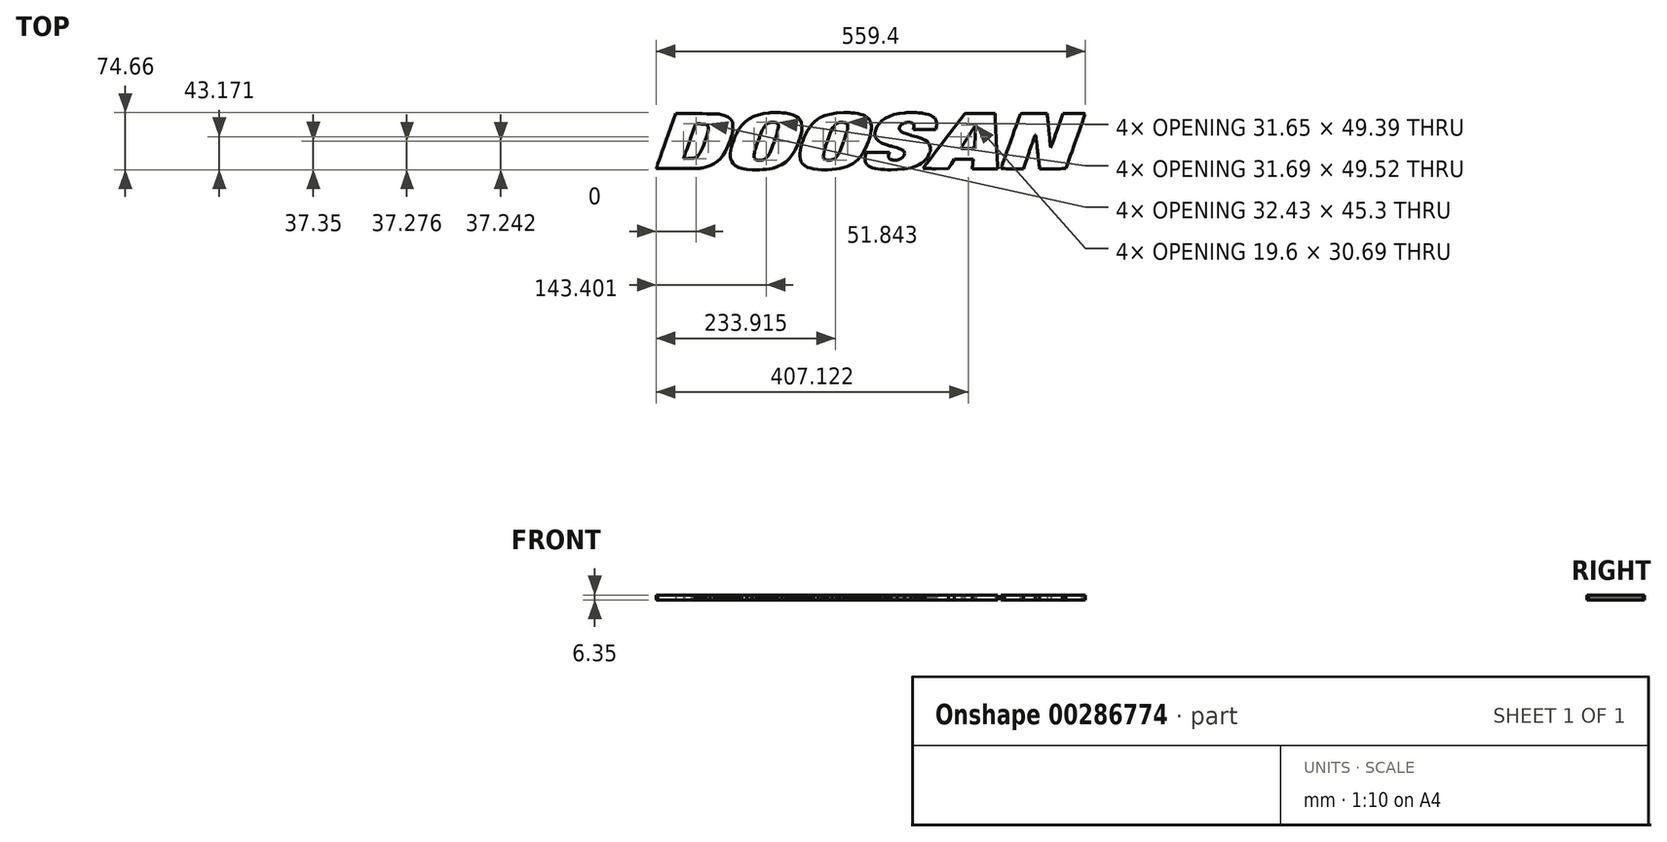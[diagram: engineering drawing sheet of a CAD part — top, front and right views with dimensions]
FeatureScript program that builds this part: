
annotation { "Feature Type Name" : "Feature", "Feature Type Description" : "" }
export const myFeature = defineFeature(function(context is Context, id is Id, definition is map)
    precondition{}
    {
        {
            var Q0;
            Q0=qCreatedBy(makeId("Top.planeOp"),FACE);
            var sketch = newSketch(context, id + "F0", { "sketchPlane" : qUnion([Q0])});
            skLineSegment(sketch, "E0", {"start": v(-105.6, 35.72) * mm, "end": v(-101.05, 34.34) * mm});
            skLineSegment(sketch, "E1", {"start": v(-101.05, 34.34) * mm, "end": v(-97.28, 32.51) * mm});
            skLineSegment(sketch, "E2", {"start": v(-97.28, 32.51) * mm, "end": v(-94.28, 30.22) * mm});
            skLineSegment(sketch, "E3", {"start": v(-94.28, 30.22) * mm, "end": v(-92.03, 27.44) * mm});
            skLineSegment(sketch, "E4", {"start": v(-92.03, 27.44) * mm, "end": v(-90.53, 24.18) * mm});
            skLineSegment(sketch, "E5", {"start": v(-90.53, 24.18) * mm, "end": v(-89.78, 20.43) * mm});
            skLineSegment(sketch, "E6", {"start": v(-89.78, 20.43) * mm, "end": v(-89.67, 17.22) * mm});
            skLineSegment(sketch, "E7", {"start": v(-89.67, 17.22) * mm, "end": v(-89.75, 16.16) * mm});
            skLineSegment(sketch, "E8", {"start": v(-89.75, 16.16) * mm, "end": v(-89.8, 15.4) * mm});
            skLineSegment(sketch, "E9", {"start": v(-89.8, 15.4) * mm, "end": v(-90.08, 13.11) * mm});
            skLineSegment(sketch, "E10", {"start": v(-90.08, 13.11) * mm, "end": v(-90.68, 9.87) * mm});
            skLineSegment(sketch, "E11", {"start": v(-90.68, 9.87) * mm, "end": v(-91.57, 6.31) * mm});
            skLineSegment(sketch, "E12", {"start": v(-91.57, 6.31) * mm, "end": v(-92.46, 3.3) * mm});
            skLineSegment(sketch, "E13", {"start": v(-92.46, 3.3) * mm, "end": v(-92.78, 2.3) * mm});
            skLineSegment(sketch, "E14", {"start": v(-92.78, 2.3) * mm, "end": v(-93.41, 0.35) * mm});
            skLineSegment(sketch, "E15", {"start": v(-93.41, 0.35) * mm, "end": v(-95.6, -5.4) * mm});
            skLineSegment(sketch, "E16", {"start": v(-95.6, -5.4) * mm, "end": v(-98.8, -12.14) * mm});
            skLineSegment(sketch, "E17", {"start": v(-98.8, -12.14) * mm, "end": v(-102.38, -17.98) * mm});
            skLineSegment(sketch, "E18", {"start": v(-102.38, -17.98) * mm, "end": v(-106.4, -22.97) * mm});
            skLineSegment(sketch, "E19", {"start": v(-106.4, -22.97) * mm, "end": v(-110.9, -27.13) * mm});
            skLineSegment(sketch, "E20", {"start": v(-110.9, -27.13) * mm, "end": v(-115.92, -30.5) * mm});
            skLineSegment(sketch, "E21", {"start": v(-115.92, -30.5) * mm, "end": v(-121.5, -33.15) * mm});
            skLineSegment(sketch, "E22", {"start": v(-121.5, -33.15) * mm, "end": v(-126.1, -34.71) * mm});
            skLineSegment(sketch, "E23", {"start": v(-126.1, -34.71) * mm, "end": v(-127.67, -35.1) * mm});
            skLineSegment(sketch, "E24", {"start": v(-127.67, -35.1) * mm, "end": v(-128.72, -35.37) * mm});
            skLineSegment(sketch, "E25", {"start": v(-128.72, -35.37) * mm, "end": v(-131.91, -36.04) * mm});
            skLineSegment(sketch, "E26", {"start": v(-131.91, -36.04) * mm, "end": v(-136.16, -36.67) * mm});
            skLineSegment(sketch, "E27", {"start": v(-136.16, -36.67) * mm, "end": v(-140.94, -37.07) * mm});
            skLineSegment(sketch, "E28", {"start": v(-140.94, -37.07) * mm, "end": v(-145.33, -37.25) * mm});
            skLineSegment(sketch, "E29", {"start": v(-145.33, -37.25) * mm, "end": v(-146.8, -37.29) * mm});
            skLineSegment(sketch, "E30", {"start": v(-146.8, -37.29) * mm, "end": v(-148.82, -37.33) * mm});
            skLineSegment(sketch, "E31", {"start": v(-148.82, -37.33) * mm, "end": v(-154.9, -37.25) * mm});
            skLineSegment(sketch, "E32", {"start": v(-154.9, -37.25) * mm, "end": v(-161.9, -36.73) * mm});
            skLineSegment(sketch, "E33", {"start": v(-161.9, -36.73) * mm, "end": v(-167.81, -35.7) * mm});
            skLineSegment(sketch, "E34", {"start": v(-167.81, -35.7) * mm, "end": v(-172.7, -34.15) * mm});
            skLineSegment(sketch, "E35", {"start": v(-172.7, -34.15) * mm, "end": v(-176.59, -32.06) * mm});
            skLineSegment(sketch, "E36", {"start": v(-176.59, -32.06) * mm, "end": v(-179.53, -29.41) * mm});
            skLineSegment(sketch, "E37", {"start": v(-179.53, -29.41) * mm, "end": v(-181.58, -26.19) * mm});
            skLineSegment(sketch, "E38", {"start": v(-181.58, -26.19) * mm, "end": v(-182.6, -23.34) * mm});
            skLineSegment(sketch, "E39", {"start": v(-182.6, -23.34) * mm, "end": v(-182.78, -22.37) * mm});
            skLineSegment(sketch, "E40", {"start": v(-182.78, -22.37) * mm, "end": v(-182.91, -21.66) * mm});
            skLineSegment(sketch, "E41", {"start": v(-182.91, -21.66) * mm, "end": v(-183.07, -19.48) * mm});
            skLineSegment(sketch, "E42", {"start": v(-183.07, -19.48) * mm, "end": v(-182.97, -16.11) * mm});
            skLineSegment(sketch, "E43", {"start": v(-182.97, -16.11) * mm, "end": v(-182.5, -12.35) * mm});
            skLineSegment(sketch, "E44", {"start": v(-182.5, -12.35) * mm, "end": v(-181.66, -8.26) * mm});
            skLineSegment(sketch, "E45", {"start": v(-181.66, -8.26) * mm, "end": v(-180.48, -3.94) * mm});
            skLineSegment(sketch, "E46", {"start": v(-180.48, -3.94) * mm, "end": v(-178.99, 0.55) * mm});
            skLineSegment(sketch, "E47", {"start": v(-178.99, 0.55) * mm, "end": v(-177.2, 5.13) * mm});
            skLineSegment(sketch, "E48", {"start": v(-177.2, 5.13) * mm, "end": v(-175.67, 8.57) * mm});
            skLineSegment(sketch, "E49", {"start": v(-175.67, 8.57) * mm, "end": v(-175.12, 9.7) * mm});
            skLineSegment(sketch, "E50", {"start": v(-175.12, 9.7) * mm, "end": v(-174.36, 11.28) * mm});
            skLineSegment(sketch, "E51", {"start": v(-174.36, 11.28) * mm, "end": v(-171.72, 15.85) * mm});
            skLineSegment(sketch, "E52", {"start": v(-171.72, 15.85) * mm, "end": v(-167.86, 21.14) * mm});
            skLineSegment(sketch, "E53", {"start": v(-167.86, 21.14) * mm, "end": v(-163.49, 25.62) * mm});
            skLineSegment(sketch, "E54", {"start": v(-163.49, 25.62) * mm, "end": v(-158.53, 29.31) * mm});
            skLineSegment(sketch, "E55", {"start": v(-158.53, 29.31) * mm, "end": v(-152.93, 32.26) * mm});
            skLineSegment(sketch, "E56", {"start": v(-152.93, 32.26) * mm, "end": v(-146.63, 34.51) * mm});
            skLineSegment(sketch, "E57", {"start": v(-146.63, 34.51) * mm, "end": v(-139.57, 36.1) * mm});
            skLineSegment(sketch, "E58", {"start": v(-139.57, 36.1) * mm, "end": v(-133.67, 36.89) * mm});
            skLineSegment(sketch, "E59", {"start": v(-133.67, 36.89) * mm, "end": v(-131.7, 37.04) * mm});
            skLineSegment(sketch, "E60", {"start": v(-131.7, 37.04) * mm, "end": v(-131.18, 37.08) * mm});
            skLineSegment(sketch, "E61", {"start": v(-131.18, 37.08) * mm, "end": v(-129.63, 37.16) * mm});
            skLineSegment(sketch, "E62", {"start": v(-129.63, 37.16) * mm, "end": v(-127.08, 37.22) * mm});
            skLineSegment(sketch, "E63", {"start": v(-127.08, 37.22) * mm, "end": v(-124.2, 37.23) * mm});
            skLineSegment(sketch, "E64", {"start": v(-124.2, 37.23) * mm, "end": v(-121.18, 37.2) * mm});
            skLineSegment(sketch, "E65", {"start": v(-121.18, 37.2) * mm, "end": v(-118.17, 37.11) * mm});
            skLineSegment(sketch, "E66", {"start": v(-118.17, 37.11) * mm, "end": v(-115.35, 37) * mm});
            skLineSegment(sketch, "E67", {"start": v(-115.35, 37) * mm, "end": v(-112.88, 36.84) * mm});
            skLineSegment(sketch, "E68", {"start": v(-112.88, 36.84) * mm, "end": v(-111.43, 36.71) * mm});
            skLineSegment(sketch, "E69", {"start": v(-111.43, 36.71) * mm, "end": v(-110.95, 36.65) * mm});
            skLineSegment(sketch, "E70", {"start": v(-25.01, 37.04) * mm, "end": v(-23.91, 36.96) * mm});
            skLineSegment(sketch, "E71", {"start": v(-23.91, 36.96) * mm, "end": v(-20.62, 36.62) * mm});
            skLineSegment(sketch, "E72", {"start": v(-20.62, 36.62) * mm, "end": v(-16.65, 36) * mm});
            skLineSegment(sketch, "E73", {"start": v(-16.65, 36) * mm, "end": v(-13.1, 35.16) * mm});
            skLineSegment(sketch, "E74", {"start": v(-13.1, 35.16) * mm, "end": v(-9.97, 34.1) * mm});
            skLineSegment(sketch, "E75", {"start": v(-9.97, 34.1) * mm, "end": v(-7.26, 32.82) * mm});
            skLineSegment(sketch, "E76", {"start": v(-7.26, 32.82) * mm, "end": v(-4.94, 31.3) * mm});
            skLineSegment(sketch, "E77", {"start": v(-4.94, 31.3) * mm, "end": v(-3.02, 29.55) * mm});
            skLineSegment(sketch, "E78", {"start": v(-3.02, 29.55) * mm, "end": v(-1.5, 27.53) * mm});
            skLineSegment(sketch, "E79", {"start": v(-1.5, 27.53) * mm, "end": v(-0.35, 25.24) * mm});
            skLineSegment(sketch, "E80", {"start": v(-0.35, 25.24) * mm, "end": v(0.41, 22.68) * mm});
            skLineSegment(sketch, "E81", {"start": v(0.41, 22.68) * mm, "end": v(0.8, 19.84) * mm});
            skLineSegment(sketch, "E82", {"start": v(0.8, 19.84) * mm, "end": v(0.81, 16.7) * mm});
            skLineSegment(sketch, "E83", {"start": v(0.81, 16.7) * mm, "end": v(0.47, 13.26) * mm});
            skLineSegment(sketch, "E84", {"start": v(0.47, 13.26) * mm, "end": v(-0.23, 9.5) * mm});
            skLineSegment(sketch, "E85", {"start": v(-0.23, 9.5) * mm, "end": v(-1.28, 5.43) * mm});
            skLineSegment(sketch, "E86", {"start": v(-1.28, 5.43) * mm, "end": v(-2.3, 2.12) * mm});
            skLineSegment(sketch, "E87", {"start": v(-2.3, 2.12) * mm, "end": v(-2.68, 1.02) * mm});
            skLineSegment(sketch, "E88", {"start": v(-2.68, 1.02) * mm, "end": v(-3.13, -0.3) * mm});
            skLineSegment(sketch, "E89", {"start": v(-3.13, -0.3) * mm, "end": v(-4.62, -4.21) * mm});
            skLineSegment(sketch, "E90", {"start": v(-4.62, -4.21) * mm, "end": v(-6.7, -9.02) * mm});
            skLineSegment(sketch, "E91", {"start": v(-6.7, -9.02) * mm, "end": v(-8.97, -13.4) * mm});
            skLineSegment(sketch, "E92", {"start": v(-8.97, -13.4) * mm, "end": v(-11.42, -17.36) * mm});
            skLineSegment(sketch, "E93", {"start": v(-11.42, -17.36) * mm, "end": v(-14.08, -20.94) * mm});
            skLineSegment(sketch, "E94", {"start": v(-14.08, -20.94) * mm, "end": v(-16.97, -24.12) * mm});
            skLineSegment(sketch, "E95", {"start": v(-16.97, -24.12) * mm, "end": v(-20.1, -26.93) * mm});
            skLineSegment(sketch, "E96", {"start": v(-20.1, -26.93) * mm, "end": v(-23.5, -29.38) * mm});
            skLineSegment(sketch, "E97", {"start": v(-23.5, -29.38) * mm, "end": v(-27.17, -31.47) * mm});
            skLineSegment(sketch, "E98", {"start": v(-27.17, -31.47) * mm, "end": v(-31.14, -33.23) * mm});
            skLineSegment(sketch, "E99", {"start": v(-31.14, -33.23) * mm, "end": v(-35.43, -34.65) * mm});
            skLineSegment(sketch, "E100", {"start": v(-35.43, -34.65) * mm, "end": v(-40.05, -35.77) * mm});
            skLineSegment(sketch, "E101", {"start": v(-40.05, -35.77) * mm, "end": v(-45.03, -36.57) * mm});
            skLineSegment(sketch, "E102", {"start": v(-45.03, -36.57) * mm, "end": v(-50.38, -37.09) * mm});
            skLineSegment(sketch, "E103", {"start": v(-50.38, -37.09) * mm, "end": v(-56.12, -37.32) * mm});
            skLineSegment(sketch, "E104", {"start": v(-56.12, -37.32) * mm, "end": v(-60.73, -37.33) * mm});
            skLineSegment(sketch, "E105", {"start": v(-60.73, -37.33) * mm, "end": v(-62.27, -37.29) * mm});
            skLineSegment(sketch, "E106", {"start": v(-62.27, -37.29) * mm, "end": v(-64, -37.24) * mm});
            skLineSegment(sketch, "E107", {"start": v(-64, -37.24) * mm, "end": v(-69.22, -36.94) * mm});
            skLineSegment(sketch, "E108", {"start": v(-69.22, -36.94) * mm, "end": v(-74.68, -36.29) * mm});
            skLineSegment(sketch, "E109", {"start": v(-74.68, -36.29) * mm, "end": v(-79.14, -35.24) * mm});
            skLineSegment(sketch, "E110", {"start": v(-79.14, -35.24) * mm, "end": v(-82.13, -34.17) * mm});
            skLineSegment(sketch, "E111", {"start": v(-82.13, -34.17) * mm, "end": v(-83.08, -33.73) * mm});
            skLineSegment(sketch, "E112", {"start": v(-83.08, -33.73) * mm, "end": v(-83.6, -33.48) * mm});
            skLineSegment(sketch, "E113", {"start": v(-83.6, -33.48) * mm, "end": v(-85.13, -32.65) * mm});
            skLineSegment(sketch, "E114", {"start": v(-85.13, -32.65) * mm, "end": v(-86.84, -31.48) * mm});
            skLineSegment(sketch, "E115", {"start": v(-86.84, -31.48) * mm, "end": v(-88.32, -30.13) * mm});
            skLineSegment(sketch, "E116", {"start": v(-88.32, -30.13) * mm, "end": v(-89.36, -28.95) * mm});
            skLineSegment(sketch, "E117", {"start": v(-89.36, -28.95) * mm, "end": v(-89.68, -28.54) * mm});
            skLineSegment(sketch, "E118", {"start": v(-89.68, -28.54) * mm, "end": v(-90.1, -27.99) * mm});
            skLineSegment(sketch, "E119", {"start": v(-90.1, -27.99) * mm, "end": v(-91.08, -26.13) * mm});
            skLineSegment(sketch, "E120", {"start": v(-91.08, -26.13) * mm, "end": v(-92, -23.28) * mm});
            skLineSegment(sketch, "E121", {"start": v(-92, -23.28) * mm, "end": v(-92.46, -19.99) * mm});
            skLineSegment(sketch, "E122", {"start": v(-92.46, -19.99) * mm, "end": v(-92.44, -16.27) * mm});
            skLineSegment(sketch, "E123", {"start": v(-92.44, -16.27) * mm, "end": v(-91.95, -12.14) * mm});
            skLineSegment(sketch, "E124", {"start": v(-91.95, -12.14) * mm, "end": v(-91, -7.6) * mm});
            skLineSegment(sketch, "E125", {"start": v(-91, -7.6) * mm, "end": v(-89.56, -2.65) * mm});
            skLineSegment(sketch, "E126", {"start": v(-89.56, -2.65) * mm, "end": v(-88.17, 1.36) * mm});
            skLineSegment(sketch, "E127", {"start": v(-88.17, 1.36) * mm, "end": v(-87.67, 2.68) * mm});
            skLineSegment(sketch, "E128", {"start": v(-87.67, 2.68) * mm, "end": v(-87.11, 4.1) * mm});
            skLineSegment(sketch, "E129", {"start": v(-87.11, 4.1) * mm, "end": v(-85.27, 8.3) * mm});
            skLineSegment(sketch, "E130", {"start": v(-85.27, 8.3) * mm, "end": v(-82.64, 13.37) * mm});
            skLineSegment(sketch, "E131", {"start": v(-82.64, 13.37) * mm, "end": v(-79.77, 17.89) * mm});
            skLineSegment(sketch, "E132", {"start": v(-79.77, 17.89) * mm, "end": v(-76.65, 21.87) * mm});
            skLineSegment(sketch, "E133", {"start": v(-76.65, 21.87) * mm, "end": v(-73.26, 25.33) * mm});
            skLineSegment(sketch, "E134", {"start": v(-73.26, 25.33) * mm, "end": v(-69.59, 28.3) * mm});
            skLineSegment(sketch, "E135", {"start": v(-69.59, 28.3) * mm, "end": v(-65.62, 30.77) * mm});
            skLineSegment(sketch, "E136", {"start": v(-65.62, 30.77) * mm, "end": v(-62.44, 32.34) * mm});
            skLineSegment(sketch, "E137", {"start": v(-62.44, 32.34) * mm, "end": v(-61.35, 32.77) * mm});
            skLineSegment(sketch, "E138", {"start": v(-61.35, 32.77) * mm, "end": v(-59.5, 33.51) * mm});
            skLineSegment(sketch, "E139", {"start": v(-59.5, 33.51) * mm, "end": v(-53.74, 35.13) * mm});
            skLineSegment(sketch, "E140", {"start": v(-53.74, 35.13) * mm, "end": v(-44.87, 36.65) * mm});
            skLineSegment(sketch, "E141", {"start": v(-44.87, 36.65) * mm, "end": v(-35.17, 37.3) * mm});
            skLineSegment(sketch, "E142", {"start": v(-35.17, 37.3) * mm, "end": v(-27.54, 37.23) * mm});
            skLineSegment(sketch, "E143", {"start": v(-27.54, 37.23) * mm, "end": v(-25.01, 37.04) * mm});
            skLineSegment(sketch, "E144", {"start": v(67.06, 36.51) * mm, "end": v(68.19, 36.37) * mm});
            skLineSegment(sketch, "E145", {"start": v(68.19, 36.37) * mm, "end": v(71.54, 35.76) * mm});
            skLineSegment(sketch, "E146", {"start": v(71.54, 35.76) * mm, "end": v(75.38, 34.76) * mm});
            skLineSegment(sketch, "E147", {"start": v(75.38, 34.76) * mm, "end": v(78.61, 33.49) * mm});
            skLineSegment(sketch, "E148", {"start": v(78.61, 33.49) * mm, "end": v(81.24, 31.94) * mm});
            skLineSegment(sketch, "E149", {"start": v(81.24, 31.94) * mm, "end": v(83.27, 30.13) * mm});
            skLineSegment(sketch, "E150", {"start": v(83.27, 30.13) * mm, "end": v(84.7, 28.02) * mm});
            skLineSegment(sketch, "E151", {"start": v(84.7, 28.02) * mm, "end": v(85.57, 25.62) * mm});
            skLineSegment(sketch, "E152", {"start": v(85.57, 25.62) * mm, "end": v(85.86, 23.6) * mm});
            skLineSegment(sketch, "E153", {"start": v(85.86, 23.6) * mm, "end": v(85.87, 22.93) * mm});
            skLineSegment(sketch, "E154", {"start": v(85.87, 22.93) * mm, "end": v(85.87, 22.62) * mm});
            skLineSegment(sketch, "E155", {"start": v(85.87, 22.62) * mm, "end": v(85.83, 21.7) * mm});
            skLineSegment(sketch, "E156", {"start": v(85.83, 21.7) * mm, "end": v(85.7, 20.31) * mm});
            skLineSegment(sketch, "E157", {"start": v(85.7, 20.31) * mm, "end": v(85.5, 18.94) * mm});
            skLineSegment(sketch, "E158", {"start": v(85.5, 18.94) * mm, "end": v(85.31, 18.04) * mm});
            skLineSegment(sketch, "E159", {"start": v(85.31, 18.04) * mm, "end": v(85.23, 17.75) * mm});
            skLineSegment(sketch, "E160", {"start": v(85.23, 17.75) * mm, "end": v(84.6, 15.17) * mm});
            skLineSegment(sketch, "E161", {"start": v(84.6, 15.17) * mm, "end": v(69.96, 15.17) * mm});
            skLineSegment(sketch, "E162", {"start": v(69.96, 15.17) * mm, "end": v(68.8, 15.17) * mm});
            skLineSegment(sketch, "E163", {"start": v(68.8, 15.17) * mm, "end": v(65.37, 15.17) * mm});
            skLineSegment(sketch, "E164", {"start": v(65.37, 15.17) * mm, "end": v(61.85, 15.18) * mm});
            skLineSegment(sketch, "E165", {"start": v(61.85, 15.18) * mm, "end": v(59.27, 15.21) * mm});
            skLineSegment(sketch, "E166", {"start": v(59.27, 15.21) * mm, "end": v(57.5, 15.26) * mm});
            skLineSegment(sketch, "E167", {"start": v(57.5, 15.26) * mm, "end": v(56.37, 15.34) * mm});
            skLineSegment(sketch, "E168", {"start": v(56.37, 15.34) * mm, "end": v(55.77, 15.45) * mm});
            skLineSegment(sketch, "E169", {"start": v(55.77, 15.45) * mm, "end": v(55.54, 15.6) * mm});
            skLineSegment(sketch, "E170", {"start": v(55.54, 15.6) * mm, "end": v(55.54, 15.76) * mm});
            skLineSegment(sketch, "E171", {"start": v(55.54, 15.76) * mm, "end": v(55.56, 15.8) * mm});
            skLineSegment(sketch, "E172", {"start": v(55.56, 15.8) * mm, "end": v(55.77, 16.3) * mm});
            skLineSegment(sketch, "E173", {"start": v(55.77, 16.3) * mm, "end": v(56.2, 17.9) * mm});
            skLineSegment(sketch, "E174", {"start": v(56.2, 17.9) * mm, "end": v(56.39, 19.84) * mm});
            skLineSegment(sketch, "E175", {"start": v(56.39, 19.84) * mm, "end": v(56.11, 21.5) * mm});
            skLineSegment(sketch, "E176", {"start": v(56.11, 21.5) * mm, "end": v(55.63, 22.5) * mm});
            skLineSegment(sketch, "E177", {"start": v(55.63, 22.5) * mm, "end": v(55.39, 22.75) * mm});
            skLineSegment(sketch, "E178", {"start": v(55.39, 22.75) * mm, "end": v(55.13, 23.03) * mm});
            skLineSegment(sketch, "E179", {"start": v(55.13, 23.03) * mm, "end": v(54.19, 23.71) * mm});
            skLineSegment(sketch, "E180", {"start": v(54.19, 23.71) * mm, "end": v(52.67, 24.33) * mm});
            skLineSegment(sketch, "E181", {"start": v(52.67, 24.33) * mm, "end": v(50.75, 24.62) * mm});
            skLineSegment(sketch, "E182", {"start": v(50.75, 24.62) * mm, "end": v(48.96, 24.65) * mm});
            skLineSegment(sketch, "E183", {"start": v(48.96, 24.65) * mm, "end": v(48.37, 24.62) * mm});
            skLineSegment(sketch, "E184", {"start": v(48.37, 24.62) * mm, "end": v(47.8, 24.6) * mm});
            skLineSegment(sketch, "E185", {"start": v(47.8, 24.6) * mm, "end": v(46.1, 24.35) * mm});
            skLineSegment(sketch, "E186", {"start": v(46.1, 24.35) * mm, "end": v(44.02, 23.8) * mm});
            skLineSegment(sketch, "E187", {"start": v(44.02, 23.8) * mm, "end": v(42.15, 23.03) * mm});
            skLineSegment(sketch, "E188", {"start": v(42.15, 23.03) * mm, "end": v(40.54, 22.04) * mm});
            skLineSegment(sketch, "E189", {"start": v(40.54, 22.04) * mm, "end": v(39.22, 20.87) * mm});
            skLineSegment(sketch, "E190", {"start": v(39.22, 20.87) * mm, "end": v(38.23, 19.54) * mm});
            skLineSegment(sketch, "E191", {"start": v(38.23, 19.54) * mm, "end": v(37.6, 18.1) * mm});
            skLineSegment(sketch, "E192", {"start": v(37.6, 18.1) * mm, "end": v(37.4, 16.93) * mm});
            skLineSegment(sketch, "E193", {"start": v(37.4, 16.93) * mm, "end": v(37.4, 16.54) * mm});
            skLineSegment(sketch, "E194", {"start": v(37.4, 16.54) * mm, "end": v(37.4, 16.22) * mm});
            skLineSegment(sketch, "E195", {"start": v(37.4, 16.22) * mm, "end": v(37.55, 15.24) * mm});
            skLineSegment(sketch, "E196", {"start": v(37.55, 15.24) * mm, "end": v(38.09, 14.07) * mm});
            skLineSegment(sketch, "E197", {"start": v(38.09, 14.07) * mm, "end": v(39.07, 12.99) * mm});
            skLineSegment(sketch, "E198", {"start": v(39.07, 12.99) * mm, "end": v(40.58, 11.96) * mm});
            skLineSegment(sketch, "E199", {"start": v(40.58, 11.96) * mm, "end": v(42.7, 10.93) * mm});
            skLineSegment(sketch, "E200", {"start": v(42.7, 10.93) * mm, "end": v(45.5, 9.86) * mm});
            skLineSegment(sketch, "E201", {"start": v(45.5, 9.86) * mm, "end": v(49.07, 8.72) * mm});
            skLineSegment(sketch, "E202", {"start": v(49.07, 8.72) * mm, "end": v(52.38, 7.75) * mm});
            skLineSegment(sketch, "E203", {"start": v(52.38, 7.75) * mm, "end": v(53.48, 7.44) * mm});
            skLineSegment(sketch, "E204", {"start": v(53.48, 7.44) * mm, "end": v(54.33, 7.2) * mm});
            skLineSegment(sketch, "E205", {"start": v(54.33, 7.2) * mm, "end": v(56.87, 6.48) * mm});
            skLineSegment(sketch, "E206", {"start": v(56.87, 6.48) * mm, "end": v(59.67, 5.67) * mm});
            skLineSegment(sketch, "E207", {"start": v(59.67, 5.67) * mm, "end": v(61.97, 4.96) * mm});
            skLineSegment(sketch, "E208", {"start": v(61.97, 4.96) * mm, "end": v(63.88, 4.33) * mm});
            skLineSegment(sketch, "E209", {"start": v(63.88, 4.33) * mm, "end": v(65.52, 3.73) * mm});
            skLineSegment(sketch, "E210", {"start": v(65.52, 3.73) * mm, "end": v(66.98, 3.12) * mm});
            skLineSegment(sketch, "E211", {"start": v(66.98, 3.12) * mm, "end": v(68.38, 2.48) * mm});
            skLineSegment(sketch, "E212", {"start": v(68.38, 2.48) * mm, "end": v(69.46, 1.95) * mm});
            skLineSegment(sketch, "E213", {"start": v(69.46, 1.95) * mm, "end": v(69.81, 1.76) * mm});
            skLineSegment(sketch, "E214", {"start": v(69.81, 1.76) * mm, "end": v(70.9, 1.2) * mm});
            skLineSegment(sketch, "E215", {"start": v(70.9, 1.2) * mm, "end": v(73.88, -1) * mm});
            skLineSegment(sketch, "E216", {"start": v(73.88, -1) * mm, "end": v(76.54, -4.3) * mm});
            skLineSegment(sketch, "E217", {"start": v(76.54, -4.3) * mm, "end": v(77.8, -8.1) * mm});
            skLineSegment(sketch, "E218", {"start": v(77.8, -8.1) * mm, "end": v(77.81, -11.37) * mm});
            skLineSegment(sketch, "E219", {"start": v(77.81, -11.37) * mm, "end": v(77.61, -12.42) * mm});
            skLineSegment(sketch, "E220", {"start": v(77.61, -12.42) * mm, "end": v(77.46, -13.21) * mm});
            skLineSegment(sketch, "E221", {"start": v(77.46, -13.21) * mm, "end": v(76.75, -15.55) * mm});
            skLineSegment(sketch, "E222", {"start": v(76.75, -15.55) * mm, "end": v(75.44, -18.56) * mm});
            skLineSegment(sketch, "E223", {"start": v(75.44, -18.56) * mm, "end": v(73.7, -21.4) * mm});
            skLineSegment(sketch, "E224", {"start": v(73.7, -21.4) * mm, "end": v(71.57, -24.07) * mm});
            skLineSegment(sketch, "E225", {"start": v(71.57, -24.07) * mm, "end": v(69.06, -26.51) * mm});
            skLineSegment(sketch, "E226", {"start": v(69.06, -26.51) * mm, "end": v(66.2, -28.72) * mm});
            skLineSegment(sketch, "E227", {"start": v(66.2, -28.72) * mm, "end": v(63.02, -30.65) * mm});
            skLineSegment(sketch, "E228", {"start": v(63.02, -30.65) * mm, "end": v(60.44, -31.92) * mm});
            skLineSegment(sketch, "E229", {"start": v(60.44, -31.92) * mm, "end": v(59.55, -32.28) * mm});
            skLineSegment(sketch, "E230", {"start": v(59.55, -32.28) * mm, "end": v(57.74, -33) * mm});
            skLineSegment(sketch, "E231", {"start": v(57.74, -33) * mm, "end": v(52.12, -34.72) * mm});
            skLineSegment(sketch, "E232", {"start": v(52.12, -34.72) * mm, "end": v(43.8, -36.34) * mm});
            skLineSegment(sketch, "E233", {"start": v(43.8, -36.34) * mm, "end": v(34.28, -37.19) * mm});
            skLineSegment(sketch, "E234", {"start": v(34.28, -37.19) * mm, "end": v(26.03, -37.35) * mm});
            skLineSegment(sketch, "E235", {"start": v(26.03, -37.35) * mm, "end": v(23.28, -37.29) * mm});
            skLineSegment(sketch, "E236", {"start": v(23.28, -37.29) * mm, "end": v(21.93, -37.26) * mm});
            skLineSegment(sketch, "E237", {"start": v(21.93, -37.26) * mm, "end": v(17.87, -37.09) * mm});
            skLineSegment(sketch, "E238", {"start": v(17.87, -37.09) * mm, "end": v(13.12, -36.74) * mm});
            skLineSegment(sketch, "E239", {"start": v(13.12, -36.74) * mm, "end": v(8.96, -36.24) * mm});
            skLineSegment(sketch, "E240", {"start": v(8.96, -36.24) * mm, "end": v(5.37, -35.57) * mm});
            skLineSegment(sketch, "E241", {"start": v(5.37, -35.57) * mm, "end": v(2.27, -34.71) * mm});
            skLineSegment(sketch, "E242", {"start": v(2.27, -34.71) * mm, "end": v(-0.37, -33.67) * mm});
            skLineSegment(sketch, "E243", {"start": v(-0.37, -33.67) * mm, "end": v(-2.6, -32.41) * mm});
            skLineSegment(sketch, "E244", {"start": v(-2.6, -32.41) * mm, "end": v(-4.04, -31.34) * mm});
            skLineSegment(sketch, "E245", {"start": v(-4.04, -31.34) * mm, "end": v(-4.48, -30.94) * mm});
            skLineSegment(sketch, "E246", {"start": v(-4.48, -30.94) * mm, "end": v(-4.9, -30.56) * mm});
            skLineSegment(sketch, "E247", {"start": v(-4.9, -30.56) * mm, "end": v(-6.02, -29.33) * mm});
            skLineSegment(sketch, "E248", {"start": v(-6.02, -29.33) * mm, "end": v(-6.97, -27.74) * mm});
            skLineSegment(sketch, "E249", {"start": v(-6.97, -27.74) * mm, "end": v(-7.45, -25.88) * mm});
            skLineSegment(sketch, "E250", {"start": v(-7.45, -25.88) * mm, "end": v(-7.59, -24.06) * mm});
            skLineSegment(sketch, "E251", {"start": v(-7.59, -24.06) * mm, "end": v(-7.59, -23.46) * mm});
            skLineSegment(sketch, "E252", {"start": v(-7.59, -23.46) * mm, "end": v(-7.59, -22.69) * mm});
            skLineSegment(sketch, "E253", {"start": v(-7.59, -22.69) * mm, "end": v(-7.4, -20.38) * mm});
            skLineSegment(sketch, "E254", {"start": v(-7.4, -20.38) * mm, "end": v(-6.9, -18.05) * mm});
            skLineSegment(sketch, "E255", {"start": v(-6.9, -18.05) * mm, "end": v(-6.74, -17.53) * mm});
            skLineSegment(sketch, "E256", {"start": v(-6.74, -17.53) * mm, "end": v(-5.86, -14.82) * mm});
            skLineSegment(sketch, "E257", {"start": v(-5.86, -14.82) * mm, "end": v(9.24, -14.82) * mm});
            skLineSegment(sketch, "E258", {"start": v(9.24, -14.82) * mm, "end": v(10.7, -14.82) * mm});
            skLineSegment(sketch, "E259", {"start": v(10.7, -14.82) * mm, "end": v(15.1, -14.82) * mm});
            skLineSegment(sketch, "E260", {"start": v(15.1, -14.82) * mm, "end": v(19.9, -14.84) * mm});
            skLineSegment(sketch, "E261", {"start": v(19.9, -14.84) * mm, "end": v(23.15, -14.86) * mm});
            skLineSegment(sketch, "E262", {"start": v(23.15, -14.86) * mm, "end": v(24.34, -14.88) * mm});
            skLineSegment(sketch, "E263", {"start": v(24.34, -14.88) * mm, "end": v(24.34, -14.89) * mm});
            skLineSegment(sketch, "E264", {"start": v(24.34, -14.89) * mm, "end": v(24.34, -15) * mm});
            skLineSegment(sketch, "E265", {"start": v(24.34, -15) * mm, "end": v(24.18, -15.38) * mm});
            skLineSegment(sketch, "E266", {"start": v(24.18, -15.38) * mm, "end": v(23.88, -16.2) * mm});
            skLineSegment(sketch, "E267", {"start": v(23.88, -16.2) * mm, "end": v(23.81, -16.4) * mm});
            skLineSegment(sketch, "E268", {"start": v(23.81, -16.4) * mm, "end": v(23.7, -16.75) * mm});
            skLineSegment(sketch, "E269", {"start": v(23.7, -16.75) * mm, "end": v(23.46, -17.84) * mm});
            skLineSegment(sketch, "E270", {"start": v(23.46, -17.84) * mm, "end": v(23.32, -19.41) * mm});
            skLineSegment(sketch, "E271", {"start": v(23.32, -19.41) * mm, "end": v(23.4, -20.89) * mm});
            skLineSegment(sketch, "E272", {"start": v(23.4, -20.89) * mm, "end": v(23.58, -21.78) * mm});
            skLineSegment(sketch, "E273", {"start": v(23.58, -21.78) * mm, "end": v(23.7, -22.05) * mm});
            skLineSegment(sketch, "E274", {"start": v(23.7, -22.05) * mm, "end": v(23.84, -22.34) * mm});
            skLineSegment(sketch, "E275", {"start": v(23.84, -22.34) * mm, "end": v(24.51, -23.1) * mm});
            skLineSegment(sketch, "E276", {"start": v(24.51, -23.1) * mm, "end": v(25.81, -23.93) * mm});
            skLineSegment(sketch, "E277", {"start": v(25.81, -23.93) * mm, "end": v(27.5, -24.5) * mm});
            skLineSegment(sketch, "E278", {"start": v(27.5, -24.5) * mm, "end": v(29.48, -24.81) * mm});
            skLineSegment(sketch, "E279", {"start": v(29.48, -24.81) * mm, "end": v(31.65, -24.86) * mm});
            skLineSegment(sketch, "E280", {"start": v(31.65, -24.86) * mm, "end": v(33.9, -24.63) * mm});
            skLineSegment(sketch, "E281", {"start": v(33.9, -24.63) * mm, "end": v(36.15, -24.12) * mm});
            skLineSegment(sketch, "E282", {"start": v(36.15, -24.12) * mm, "end": v(37.76, -23.56) * mm});
            skLineSegment(sketch, "E283", {"start": v(37.76, -23.56) * mm, "end": v(38.28, -23.32) * mm});
            skLineSegment(sketch, "E284", {"start": v(38.28, -23.32) * mm, "end": v(39.15, -22.91) * mm});
            skLineSegment(sketch, "E285", {"start": v(39.15, -22.91) * mm, "end": v(41.52, -21.16) * mm});
            skLineSegment(sketch, "E286", {"start": v(41.52, -21.16) * mm, "end": v(43.5, -18.5) * mm});
            skLineSegment(sketch, "E287", {"start": v(43.5, -18.5) * mm, "end": v(44.06, -15.72) * mm});
            skLineSegment(sketch, "E288", {"start": v(44.06, -15.72) * mm, "end": v(43.43, -13.71) * mm});
            skLineSegment(sketch, "E289", {"start": v(43.43, -13.71) * mm, "end": v(43, -13.23) * mm});
            skLineSegment(sketch, "E290", {"start": v(43, -13.23) * mm, "end": v(42.8, -13) * mm});
            skLineSegment(sketch, "E291", {"start": v(42.8, -13) * mm, "end": v(42.15, -12.36) * mm});
            skLineSegment(sketch, "E292", {"start": v(42.15, -12.36) * mm, "end": v(41.17, -11.59) * mm});
            skLineSegment(sketch, "E293", {"start": v(41.17, -11.59) * mm, "end": v(39.96, -10.87) * mm});
            skLineSegment(sketch, "E294", {"start": v(39.96, -10.87) * mm, "end": v(38.43, -10.16) * mm});
            skLineSegment(sketch, "E295", {"start": v(38.43, -10.16) * mm, "end": v(36.48, -9.42) * mm});
            skLineSegment(sketch, "E296", {"start": v(36.48, -9.42) * mm, "end": v(34.02, -8.63) * mm});
            skLineSegment(sketch, "E297", {"start": v(34.02, -8.63) * mm, "end": v(30.95, -7.72) * mm});
            skLineSegment(sketch, "E298", {"start": v(30.95, -7.72) * mm, "end": v(28.1, -6.92) * mm});
            skLineSegment(sketch, "E299", {"start": v(28.1, -6.92) * mm, "end": v(27.16, -6.67) * mm});
            skLineSegment(sketch, "E300", {"start": v(27.16, -6.67) * mm, "end": v(25.34, -6.17) * mm});
            skLineSegment(sketch, "E301", {"start": v(25.34, -6.17) * mm, "end": v(19.9, -4.49) * mm});
            skLineSegment(sketch, "E302", {"start": v(19.9, -4.49) * mm, "end": v(14.52, -2.39) * mm});
            skLineSegment(sketch, "E303", {"start": v(14.52, -2.39) * mm, "end": v(10.63, -0.2) * mm});
            skLineSegment(sketch, "E304", {"start": v(10.63, -0.2) * mm, "end": v(8.47, 1.57) * mm});
            skLineSegment(sketch, "E305", {"start": v(8.47, 1.57) * mm, "end": v(7.87, 2.26) * mm});
            skLineSegment(sketch, "E306", {"start": v(7.87, 2.26) * mm, "end": v(7.39, 2.8) * mm});
            skLineSegment(sketch, "E307", {"start": v(7.39, 2.8) * mm, "end": v(6.26, 4.7) * mm});
            skLineSegment(sketch, "E308", {"start": v(6.26, 4.7) * mm, "end": v(5.41, 7.5) * mm});
            skLineSegment(sketch, "E309", {"start": v(5.41, 7.5) * mm, "end": v(5.34, 10.6) * mm});
            skLineSegment(sketch, "E310", {"start": v(5.34, 10.6) * mm, "end": v(5.78, 13.15) * mm});
            skLineSegment(sketch, "E311", {"start": v(5.78, 13.15) * mm, "end": v(6.03, 13.97) * mm});
            skLineSegment(sketch, "E312", {"start": v(6.03, 13.97) * mm, "end": v(6.4, 15.2) * mm});
            skLineSegment(sketch, "E313", {"start": v(6.4, 15.2) * mm, "end": v(8, 18.77) * mm});
            skLineSegment(sketch, "E314", {"start": v(8, 18.77) * mm, "end": v(10.81, 23.02) * mm});
            skLineSegment(sketch, "E315", {"start": v(10.81, 23.02) * mm, "end": v(14.46, 26.72) * mm});
            skLineSegment(sketch, "E316", {"start": v(14.46, 26.72) * mm, "end": v(18.94, 29.89) * mm});
            skLineSegment(sketch, "E317", {"start": v(18.94, 29.89) * mm, "end": v(24.26, 32.5) * mm});
            skLineSegment(sketch, "E318", {"start": v(24.26, 32.5) * mm, "end": v(30.41, 34.56) * mm});
            skLineSegment(sketch, "E319", {"start": v(30.41, 34.56) * mm, "end": v(37.39, 36.08) * mm});
            skLineSegment(sketch, "E320", {"start": v(37.39, 36.08) * mm, "end": v(43.23, 36.88) * mm});
            skLineSegment(sketch, "E321", {"start": v(43.23, 36.88) * mm, "end": v(45.2, 37.04) * mm});
            skLineSegment(sketch, "E322", {"start": v(45.2, 37.04) * mm, "end": v(45.73, 37.09) * mm});
            skLineSegment(sketch, "E323", {"start": v(45.73, 37.09) * mm, "end": v(47.36, 37.17) * mm});
            skLineSegment(sketch, "E324", {"start": v(47.36, 37.17) * mm, "end": v(50.02, 37.23) * mm});
            skLineSegment(sketch, "E325", {"start": v(50.02, 37.23) * mm, "end": v(53, 37.24) * mm});
            skLineSegment(sketch, "E326", {"start": v(53, 37.24) * mm, "end": v(56.14, 37.19) * mm});
            skLineSegment(sketch, "E327", {"start": v(56.14, 37.19) * mm, "end": v(59.28, 37.09) * mm});
            skLineSegment(sketch, "E328", {"start": v(59.28, 37.09) * mm, "end": v(62.25, 36.94) * mm});
            skLineSegment(sketch, "E329", {"start": v(62.25, 36.94) * mm, "end": v(64.9, 36.75) * mm});
            skLineSegment(sketch, "E330", {"start": v(64.9, 36.75) * mm, "end": v(66.52, 36.59) * mm});
            skLineSegment(sketch, "E331", {"start": v(66.52, 36.59) * mm, "end": v(67.06, 36.51) * mm});
            skLineSegment(sketch, "E332", {"start": v(-197.56, 35.17) * mm, "end": v(-196.01, 34.9) * mm});
            skLineSegment(sketch, "E333", {"start": v(-196.01, 34.9) * mm, "end": v(-191.44, 33.75) * mm});
            skLineSegment(sketch, "E334", {"start": v(-191.44, 33.75) * mm, "end": v(-186.71, 31.76) * mm});
            skLineSegment(sketch, "E335", {"start": v(-186.71, 31.76) * mm, "end": v(-183.23, 29.14) * mm});
            skLineSegment(sketch, "E336", {"start": v(-183.23, 29.14) * mm, "end": v(-181.32, 26.7) * mm});
            skLineSegment(sketch, "E337", {"start": v(-181.32, 26.7) * mm, "end": v(-180.87, 25.79) * mm});
            skLineSegment(sketch, "E338", {"start": v(-180.87, 25.79) * mm, "end": v(-180.7, 25.44) * mm});
            skLineSegment(sketch, "E339", {"start": v(-180.7, 25.44) * mm, "end": v(-180.22, 24.37) * mm});
            skLineSegment(sketch, "E340", {"start": v(-180.22, 24.37) * mm, "end": v(-179.88, 23.12) * mm});
            skLineSegment(sketch, "E341", {"start": v(-179.88, 23.12) * mm, "end": v(-179.76, 21.39) * mm});
            skLineSegment(sketch, "E342", {"start": v(-179.76, 21.39) * mm, "end": v(-179.74, 19.24) * mm});
            skLineSegment(sketch, "E343", {"start": v(-179.74, 19.24) * mm, "end": v(-179.74, 18.52) * mm});
            skLineSegment(sketch, "E344", {"start": v(-179.74, 18.52) * mm, "end": v(-179.75, 17.85) * mm});
            skLineSegment(sketch, "E345", {"start": v(-179.75, 17.85) * mm, "end": v(-179.8, 15.83) * mm});
            skLineSegment(sketch, "E346", {"start": v(-179.8, 15.83) * mm, "end": v(-179.94, 13.82) * mm});
            skLineSegment(sketch, "E347", {"start": v(-179.94, 13.82) * mm, "end": v(-180.24, 12.02) * mm});
            skLineSegment(sketch, "E348", {"start": v(-180.24, 12.02) * mm, "end": v(-180.6, 10.49) * mm});
            skLineSegment(sketch, "E349", {"start": v(-180.6, 10.49) * mm, "end": v(-180.73, 9.98) * mm});
            skLineSegment(sketch, "E350", {"start": v(-180.73, 9.98) * mm, "end": v(-180.98, 9.02) * mm});
            skLineSegment(sketch, "E351", {"start": v(-180.98, 9.02) * mm, "end": v(-181.86, 6.16) * mm});
            skLineSegment(sketch, "E352", {"start": v(-181.86, 6.16) * mm, "end": v(-183.43, 1.41) * mm});
            skLineSegment(sketch, "E353", {"start": v(-183.43, 1.41) * mm, "end": v(-185.15, -3.44) * mm});
            skLineSegment(sketch, "E354", {"start": v(-185.15, -3.44) * mm, "end": v(-186.34, -6.56) * mm});
            skLineSegment(sketch, "E355", {"start": v(-186.34, -6.56) * mm, "end": v(-186.76, -7.58) * mm});
            skLineSegment(sketch, "E356", {"start": v(-186.76, -7.58) * mm, "end": v(-187.38, -9.08) * mm});
            skLineSegment(sketch, "E357", {"start": v(-187.38, -9.08) * mm, "end": v(-189.48, -13.45) * mm});
            skLineSegment(sketch, "E358", {"start": v(-189.48, -13.45) * mm, "end": v(-192.52, -18.5) * mm});
            skLineSegment(sketch, "E359", {"start": v(-192.52, -18.5) * mm, "end": v(-195.93, -22.81) * mm});
            skLineSegment(sketch, "E360", {"start": v(-195.93, -22.81) * mm, "end": v(-199.8, -26.43) * mm});
            skLineSegment(sketch, "E361", {"start": v(-199.8, -26.43) * mm, "end": v(-204.18, -29.42) * mm});
            skLineSegment(sketch, "E362", {"start": v(-204.18, -29.42) * mm, "end": v(-209.17, -31.83) * mm});
            skLineSegment(sketch, "E363", {"start": v(-209.17, -31.83) * mm, "end": v(-214.81, -33.73) * mm});
            skLineSegment(sketch, "E364", {"start": v(-214.81, -33.73) * mm, "end": v(-219.59, -34.88) * mm});
            skLineSegment(sketch, "E365", {"start": v(-219.59, -34.88) * mm, "end": v(-221.2, -35.17) * mm});
            skLineSegment(sketch, "E366", {"start": v(-221.2, -35.17) * mm, "end": v(-221.49, -35.22) * mm});
            skLineSegment(sketch, "E367", {"start": v(-221.49, -35.22) * mm, "end": v(-222.37, -35.35) * mm});
            skLineSegment(sketch, "E368", {"start": v(-222.37, -35.35) * mm, "end": v(-223.86, -35.49) * mm});
            skLineSegment(sketch, "E369", {"start": v(-223.86, -35.49) * mm, "end": v(-225.9, -35.6) * mm});
            skLineSegment(sketch, "E370", {"start": v(-225.9, -35.6) * mm, "end": v(-228.7, -35.68) * mm});
            skLineSegment(sketch, "E371", {"start": v(-228.7, -35.68) * mm, "end": v(-232.5, -35.75) * mm});
            skLineSegment(sketch, "E372", {"start": v(-232.5, -35.75) * mm, "end": v(-237.51, -35.8) * mm});
            skLineSegment(sketch, "E373", {"start": v(-237.51, -35.8) * mm, "end": v(-243.98, -35.84) * mm});
            skLineSegment(sketch, "E374", {"start": v(-243.98, -35.84) * mm, "end": v(-250.1, -35.87) * mm});
            skLineSegment(sketch, "E375", {"start": v(-250.1, -35.87) * mm, "end": v(-252.13, -35.88) * mm});
            skLineSegment(sketch, "E376", {"start": v(-252.13, -35.88) * mm, "end": v(-253.52, -35.88) * mm});
            skLineSegment(sketch, "E377", {"start": v(-253.52, -35.88) * mm, "end": v(-257.68, -35.9) * mm});
            skLineSegment(sketch, "E378", {"start": v(-257.68, -35.9) * mm, "end": v(-262.86, -35.9) * mm});
            skLineSegment(sketch, "E379", {"start": v(-262.86, -35.9) * mm, "end": v(-267.55, -35.9) * mm});
            skLineSegment(sketch, "E380", {"start": v(-267.55, -35.9) * mm, "end": v(-271.64, -35.89) * mm});
            skLineSegment(sketch, "E381", {"start": v(-271.64, -35.89) * mm, "end": v(-275.02, -35.86) * mm});
            skLineSegment(sketch, "E382", {"start": v(-275.02, -35.86) * mm, "end": v(-277.58, -35.83) * mm});
            skLineSegment(sketch, "E383", {"start": v(-277.58, -35.83) * mm, "end": v(-279.2, -35.78) * mm});
            skLineSegment(sketch, "E384", {"start": v(-279.2, -35.78) * mm, "end": v(-279.75, -35.75) * mm});
            skLineSegment(sketch, "E385", {"start": v(-279.75, -35.75) * mm, "end": v(-279.75, -35.74) * mm});
            skLineSegment(sketch, "E386", {"start": v(-279.75, -35.74) * mm, "end": v(-279.75, -35.54) * mm});
            skLineSegment(sketch, "E387", {"start": v(-279.75, -35.54) * mm, "end": v(-279.5, -34.95) * mm});
            skLineSegment(sketch, "E388", {"start": v(-279.5, -34.95) * mm, "end": v(-278.76, -32.81) * mm});
            skLineSegment(sketch, "E389", {"start": v(-278.76, -32.81) * mm, "end": v(-277.6, -29.46) * mm});
            skLineSegment(sketch, "E390", {"start": v(-277.6, -29.46) * mm, "end": v(-276.05, -25.04) * mm});
            skLineSegment(sketch, "E391", {"start": v(-276.05, -25.04) * mm, "end": v(-274.18, -19.71) * mm});
            skLineSegment(sketch, "E392", {"start": v(-274.18, -19.71) * mm, "end": v(-272.04, -13.61) * mm});
            skLineSegment(sketch, "E393", {"start": v(-272.04, -13.61) * mm, "end": v(-269.69, -6.9) * mm});
            skLineSegment(sketch, "E394", {"start": v(-269.69, -6.9) * mm, "end": v(-267.8, -1.51) * mm});
            skLineSegment(sketch, "E395", {"start": v(-267.8, -1.51) * mm, "end": v(-267.16, 0.28) * mm});
            skLineSegment(sketch, "E396", {"start": v(-267.16, 0.28) * mm, "end": v(-254.53, 36.02) * mm});
            skLineSegment(sketch, "E397", {"start": v(-254.53, 36.02) * mm, "end": v(-227.72, 35.88) * mm});
            skLineSegment(sketch, "E398", {"start": v(-227.72, 35.88) * mm, "end": v(-225.8, 35.87) * mm});
            skLineSegment(sketch, "E399", {"start": v(-225.8, 35.87) * mm, "end": v(-220.04, 35.84) * mm});
            skLineSegment(sketch, "E400", {"start": v(-220.04, 35.84) * mm, "end": v(-213.85, 35.8) * mm});
            skLineSegment(sketch, "E401", {"start": v(-213.85, 35.8) * mm, "end": v(-208.97, 35.74) * mm});
            skLineSegment(sketch, "E402", {"start": v(-208.97, 35.74) * mm, "end": v(-205.2, 35.67) * mm});
            skLineSegment(sketch, "E403", {"start": v(-205.2, 35.67) * mm, "end": v(-202.37, 35.59) * mm});
            skLineSegment(sketch, "E404", {"start": v(-202.37, 35.59) * mm, "end": v(-200.27, 35.48) * mm});
            skLineSegment(sketch, "E405", {"start": v(-200.27, 35.48) * mm, "end": v(-198.73, 35.34) * mm});
            skLineSegment(sketch, "E406", {"start": v(-198.73, 35.34) * mm, "end": v(-197.85, 35.22) * mm});
            skLineSegment(sketch, "E407", {"start": v(-197.85, 35.22) * mm, "end": v(-197.56, 35.17) * mm});
            skLineSegment(sketch, "E408", {"start": v(161.92, 34.64) * mm, "end": v(161.92, 34.4) * mm});
            skLineSegment(sketch, "E409", {"start": v(161.92, 34.4) * mm, "end": v(161.96, 33.67) * mm});
            skLineSegment(sketch, "E410", {"start": v(161.96, 33.67) * mm, "end": v(162.07, 31.43) * mm});
            skLineSegment(sketch, "E411", {"start": v(162.07, 31.43) * mm, "end": v(162.23, 28.08) * mm});
            skLineSegment(sketch, "E412", {"start": v(162.23, 28.08) * mm, "end": v(162.45, 23.74) * mm});
            skLineSegment(sketch, "E413", {"start": v(162.45, 23.74) * mm, "end": v(162.71, 18.56) * mm});
            skLineSegment(sketch, "E414", {"start": v(162.71, 18.56) * mm, "end": v(163.01, 12.7) * mm});
            skLineSegment(sketch, "E415", {"start": v(163.01, 12.7) * mm, "end": v(163.34, 6.29) * mm});
            skLineSegment(sketch, "E416", {"start": v(163.34, 6.29) * mm, "end": v(163.6, 1.18) * mm});
            skLineSegment(sketch, "E417", {"start": v(163.6, 1.18) * mm, "end": v(163.69, -0.53) * mm});
            skLineSegment(sketch, "E418", {"start": v(163.69, -0.53) * mm, "end": v(163.78, -2.23) * mm});
            skLineSegment(sketch, "E419", {"start": v(163.78, -2.23) * mm, "end": v(164.05, -7.34) * mm});
            skLineSegment(sketch, "E420", {"start": v(164.05, -7.34) * mm, "end": v(164.38, -13.72) * mm});
            skLineSegment(sketch, "E421", {"start": v(164.38, -13.72) * mm, "end": v(164.68, -19.54) * mm});
            skLineSegment(sketch, "E422", {"start": v(164.68, -19.54) * mm, "end": v(164.94, -24.65) * mm});
            skLineSegment(sketch, "E423", {"start": v(164.94, -24.65) * mm, "end": v(165.16, -28.9) * mm});
            skLineSegment(sketch, "E424", {"start": v(165.16, -28.9) * mm, "end": v(165.31, -32.18) * mm});
            skLineSegment(sketch, "E425", {"start": v(165.31, -32.18) * mm, "end": v(165.42, -34.31) * mm});
            skLineSegment(sketch, "E426", {"start": v(165.42, -34.31) * mm, "end": v(165.45, -34.96) * mm});
            skLineSegment(sketch, "E427", {"start": v(165.45, -34.96) * mm, "end": v(165.45, -35.17) * mm});
            skLineSegment(sketch, "E428", {"start": v(165.45, -35.17) * mm, "end": v(165.45, -35.98) * mm});
            skLineSegment(sketch, "E429", {"start": v(165.45, -35.98) * mm, "end": v(132.3, -35.98) * mm});
            skLineSegment(sketch, "E430", {"start": v(132.3, -35.98) * mm, "end": v(132.43, -35.17) * mm});
            skLineSegment(sketch, "E431", {"start": v(132.43, -35.17) * mm, "end": v(132.46, -35.07) * mm});
            skLineSegment(sketch, "E432", {"start": v(132.46, -35.07) * mm, "end": v(132.53, -34.54) * mm});
            skLineSegment(sketch, "E433", {"start": v(132.53, -34.54) * mm, "end": v(132.68, -33.38) * mm});
            skLineSegment(sketch, "E434", {"start": v(132.68, -33.38) * mm, "end": v(132.84, -31.87) * mm});
            skLineSegment(sketch, "E435", {"start": v(132.84, -31.87) * mm, "end": v(132.96, -30.59) * mm});
            skLineSegment(sketch, "E436", {"start": v(132.96, -30.59) * mm, "end": v(133, -30.16) * mm});
            skLineSegment(sketch, "E437", {"start": v(133, -30.16) * mm, "end": v(133.04, -29.72) * mm});
            skLineSegment(sketch, "E438", {"start": v(133.04, -29.72) * mm, "end": v(133.16, -28.41) * mm});
            skLineSegment(sketch, "E439", {"start": v(133.16, -28.41) * mm, "end": v(133.32, -26.78) * mm});
            skLineSegment(sketch, "E440", {"start": v(133.32, -26.78) * mm, "end": v(133.46, -25.46) * mm});
            skLineSegment(sketch, "E441", {"start": v(133.46, -25.46) * mm, "end": v(133.53, -24.8) * mm});
            skLineSegment(sketch, "E442", {"start": v(133.53, -24.8) * mm, "end": v(133.56, -24.62) * mm});
            skLineSegment(sketch, "E443", {"start": v(133.56, -24.62) * mm, "end": v(133.77, -23.28) * mm});
            skLineSegment(sketch, "E444", {"start": v(133.77, -23.28) * mm, "end": v(108.7, -23.28) * mm});
            skLineSegment(sketch, "E445", {"start": v(108.7, -23.28) * mm, "end": v(104.88, -29.63) * mm});
            skLineSegment(sketch, "E446", {"start": v(104.88, -29.63) * mm, "end": v(101.07, -35.95) * mm});
            skLineSegment(sketch, "E447", {"start": v(101.07, -35.95) * mm, "end": v(84.56, -35.98) * mm});
            skLineSegment(sketch, "E448", {"start": v(84.56, -35.98) * mm, "end": v(83.73, -35.98) * mm});
            skLineSegment(sketch, "E449", {"start": v(83.73, -35.98) * mm, "end": v(81.24, -35.98) * mm});
            skLineSegment(sketch, "E450", {"start": v(81.24, -35.98) * mm, "end": v(78.15, -35.96) * mm});
            skLineSegment(sketch, "E451", {"start": v(78.15, -35.96) * mm, "end": v(75.35, -35.93) * mm});
            skLineSegment(sketch, "E452", {"start": v(75.35, -35.93) * mm, "end": v(72.92, -35.9) * mm});
            skLineSegment(sketch, "E453", {"start": v(72.92, -35.9) * mm, "end": v(70.92, -35.85) * mm});
            skLineSegment(sketch, "E454", {"start": v(70.92, -35.85) * mm, "end": v(69.4, -35.8) * mm});
            skLineSegment(sketch, "E455", {"start": v(69.4, -35.8) * mm, "end": v(68.47, -35.75) * mm});
            skLineSegment(sketch, "E456", {"start": v(68.47, -35.75) * mm, "end": v(68.16, -35.7) * mm});
            skLineSegment(sketch, "E457", {"start": v(68.16, -35.7) * mm, "end": v(68.17, -35.66) * mm});
            skLineSegment(sketch, "E458", {"start": v(68.17, -35.66) * mm, "end": v(68.73, -34.9) * mm});
            skLineSegment(sketch, "E459", {"start": v(68.73, -34.9) * mm, "end": v(70.34, -32.76) * mm});
            skLineSegment(sketch, "E460", {"start": v(70.34, -32.76) * mm, "end": v(72.87, -29.4) * mm});
            skLineSegment(sketch, "E461", {"start": v(72.87, -29.4) * mm, "end": v(76.2, -25) * mm});
            skLineSegment(sketch, "E462", {"start": v(76.2, -25) * mm, "end": v(80.24, -19.68) * mm});
            skLineSegment(sketch, "E463", {"start": v(80.24, -19.68) * mm, "end": v(84.86, -13.59) * mm});
            skLineSegment(sketch, "E464", {"start": v(84.86, -13.59) * mm, "end": v(89.96, -6.89) * mm});
            skLineSegment(sketch, "E465", {"start": v(89.96, -6.89) * mm, "end": v(94.06, -1.5) * mm});
            skLineSegment(sketch, "E466", {"start": v(94.06, -1.5) * mm, "end": v(95.43, 0.28) * mm});
            skLineSegment(sketch, "E467", {"start": v(95.43, 0.28) * mm, "end": v(122.55, 35.98) * mm});
            skLineSegment(sketch, "E468", {"start": v(122.55, 35.98) * mm, "end": v(161.92, 35.98) * mm});
            skLineSegment(sketch, "E469", {"start": v(161.92, 35.98) * mm, "end": v(161.92, 34.64) * mm});
            skLineSegment(sketch, "E470", {"start": v(230.12, 34.5) * mm, "end": v(230.14, 34.32) * mm});
            skLineSegment(sketch, "E471", {"start": v(230.14, 34.32) * mm, "end": v(230.2, 33.77) * mm});
            skLineSegment(sketch, "E472", {"start": v(230.2, 33.77) * mm, "end": v(230.35, 32.27) * mm});
            skLineSegment(sketch, "E473", {"start": v(230.35, 32.27) * mm, "end": v(230.57, 30.1) * mm});
            skLineSegment(sketch, "E474", {"start": v(230.57, 30.1) * mm, "end": v(230.84, 27.34) * mm});
            skLineSegment(sketch, "E475", {"start": v(230.84, 27.34) * mm, "end": v(231.17, 24.09) * mm});
            skLineSegment(sketch, "E476", {"start": v(231.17, 24.09) * mm, "end": v(231.53, 20.42) * mm});
            skLineSegment(sketch, "E477", {"start": v(231.53, 20.42) * mm, "end": v(231.92, 16.45) * mm});
            skLineSegment(sketch, "E478", {"start": v(231.92, 16.45) * mm, "end": v(232.23, 13.3) * mm});
            skLineSegment(sketch, "E479", {"start": v(232.23, 13.3) * mm, "end": v(232.34, 12.24) * mm});
            skLineSegment(sketch, "E480", {"start": v(232.34, 12.24) * mm, "end": v(232.44, 11.2) * mm});
            skLineSegment(sketch, "E481", {"start": v(232.44, 11.2) * mm, "end": v(232.76, 8.08) * mm});
            skLineSegment(sketch, "E482", {"start": v(232.76, 8.08) * mm, "end": v(233.17, 4.2) * mm});
            skLineSegment(sketch, "E483", {"start": v(233.17, 4.2) * mm, "end": v(233.55, 0.7) * mm});
            skLineSegment(sketch, "E484", {"start": v(233.55, 0.7) * mm, "end": v(233.9, -2.36) * mm});
            skLineSegment(sketch, "E485", {"start": v(233.9, -2.36) * mm, "end": v(234.2, -4.88) * mm});
            skLineSegment(sketch, "E486", {"start": v(234.2, -4.88) * mm, "end": v(234.43, -6.77) * mm});
            skLineSegment(sketch, "E487", {"start": v(234.43, -6.77) * mm, "end": v(234.6, -7.96) * mm});
            skLineSegment(sketch, "E488", {"start": v(234.6, -7.96) * mm, "end": v(234.7, -8.36) * mm});
            skLineSegment(sketch, "E489", {"start": v(234.7, -8.36) * mm, "end": v(234.75, -8.35) * mm});
            skLineSegment(sketch, "E490", {"start": v(234.75, -8.35) * mm, "end": v(234.93, -7.9) * mm});
            skLineSegment(sketch, "E491", {"start": v(234.93, -7.9) * mm, "end": v(235.44, -6.58) * mm});
            skLineSegment(sketch, "E492", {"start": v(235.44, -6.58) * mm, "end": v(236.22, -4.52) * mm});
            skLineSegment(sketch, "E493", {"start": v(236.22, -4.52) * mm, "end": v(237.23, -1.8) * mm});
            skLineSegment(sketch, "E494", {"start": v(237.23, -1.8) * mm, "end": v(238.43, 1.5) * mm});
            skLineSegment(sketch, "E495", {"start": v(238.43, 1.5) * mm, "end": v(239.78, 5.26) * mm});
            skLineSegment(sketch, "E496", {"start": v(239.78, 5.26) * mm, "end": v(241.27, 9.42) * mm});
            skLineSegment(sketch, "E497", {"start": v(241.27, 9.42) * mm, "end": v(242.46, 12.75) * mm});
            skLineSegment(sketch, "E498", {"start": v(242.46, 12.75) * mm, "end": v(242.85, 13.86) * mm});
            skLineSegment(sketch, "E499", {"start": v(242.85, 13.86) * mm, "end": v(250.65, 35.98) * mm});
            skLineSegment(sketch, "E500", {"start": v(250.65, 35.98) * mm, "end": v(265.25, 35.98) * mm});
            skLineSegment(sketch, "E501", {"start": v(265.25, 35.98) * mm, "end": v(266.23, 35.98) * mm});
            skLineSegment(sketch, "E502", {"start": v(266.23, 35.98) * mm, "end": v(269.18, 35.98) * mm});
            skLineSegment(sketch, "E503", {"start": v(269.18, 35.98) * mm, "end": v(272.37, 35.96) * mm});
            skLineSegment(sketch, "E504", {"start": v(272.37, 35.96) * mm, "end": v(274.9, 35.93) * mm});
            skLineSegment(sketch, "E505", {"start": v(274.9, 35.93) * mm, "end": v(276.81, 35.9) * mm});
            skLineSegment(sketch, "E506", {"start": v(276.81, 35.9) * mm, "end": v(278.19, 35.83) * mm});
            skLineSegment(sketch, "E507", {"start": v(278.19, 35.83) * mm, "end": v(279.08, 35.76) * mm});
            skLineSegment(sketch, "E508", {"start": v(279.08, 35.76) * mm, "end": v(279.54, 35.67) * mm});
            skLineSegment(sketch, "E509", {"start": v(279.54, 35.67) * mm, "end": v(279.65, 35.57) * mm});
            skLineSegment(sketch, "E510", {"start": v(279.65, 35.57) * mm, "end": v(279.65, 35.56) * mm});
            skLineSegment(sketch, "E511", {"start": v(279.65, 35.56) * mm, "end": v(279.63, 35.5) * mm});
            skLineSegment(sketch, "E512", {"start": v(279.63, 35.5) * mm, "end": v(279.37, 34.76) * mm});
            skLineSegment(sketch, "E513", {"start": v(279.37, 34.76) * mm, "end": v(278.62, 32.63) * mm});
            skLineSegment(sketch, "E514", {"start": v(278.62, 32.63) * mm, "end": v(277.45, 29.33) * mm});
            skLineSegment(sketch, "E515", {"start": v(277.45, 29.33) * mm, "end": v(275.91, 24.99) * mm});
            skLineSegment(sketch, "E516", {"start": v(275.91, 24.99) * mm, "end": v(274.06, 19.76) * mm});
            skLineSegment(sketch, "E517", {"start": v(274.06, 19.76) * mm, "end": v(271.94, 13.78) * mm});
            skLineSegment(sketch, "E518", {"start": v(271.94, 13.78) * mm, "end": v(269.61, 7.2) * mm});
            skLineSegment(sketch, "E519", {"start": v(269.61, 7.2) * mm, "end": v(267.74, 1.93) * mm});
            skLineSegment(sketch, "E520", {"start": v(267.74, 1.93) * mm, "end": v(267.12, 0.18) * mm});
            skLineSegment(sketch, "E521", {"start": v(267.12, 0.18) * mm, "end": v(266.5, -1.58) * mm});
            skLineSegment(sketch, "E522", {"start": v(266.5, -1.58) * mm, "end": v(264.63, -6.86) * mm});
            skLineSegment(sketch, "E523", {"start": v(264.63, -6.86) * mm, "end": v(262.3, -13.44) * mm});
            skLineSegment(sketch, "E524", {"start": v(262.3, -13.44) * mm, "end": v(260.17, -19.43) * mm});
            skLineSegment(sketch, "E525", {"start": v(260.17, -19.43) * mm, "end": v(258.31, -24.68) * mm});
            skLineSegment(sketch, "E526", {"start": v(258.31, -24.68) * mm, "end": v(256.76, -29.04) * mm});
            skLineSegment(sketch, "E527", {"start": v(256.76, -29.04) * mm, "end": v(255.58, -32.37) * mm});
            skLineSegment(sketch, "E528", {"start": v(255.58, -32.37) * mm, "end": v(254.82, -34.52) * mm});
            skLineSegment(sketch, "E529", {"start": v(254.82, -34.52) * mm, "end": v(254.55, -35.27) * mm});
            skLineSegment(sketch, "E530", {"start": v(254.55, -35.27) * mm, "end": v(254.53, -35.35) * mm});
            skLineSegment(sketch, "E531", {"start": v(254.53, -35.35) * mm, "end": v(254.5, -35.4) * mm});
            skLineSegment(sketch, "E532", {"start": v(254.5, -35.4) * mm, "end": v(254.37, -35.55) * mm});
            skLineSegment(sketch, "E533", {"start": v(254.37, -35.55) * mm, "end": v(253.96, -35.7) * mm});
            skLineSegment(sketch, "E534", {"start": v(253.96, -35.7) * mm, "end": v(253.15, -35.81) * mm});
            skLineSegment(sketch, "E535", {"start": v(253.15, -35.81) * mm, "end": v(251.76, -35.89) * mm});
            skLineSegment(sketch, "E536", {"start": v(251.76, -35.89) * mm, "end": v(249.64, -35.94) * mm});
            skLineSegment(sketch, "E537", {"start": v(249.64, -35.94) * mm, "end": v(246.62, -35.97) * mm});
            skLineSegment(sketch, "E538", {"start": v(246.62, -35.97) * mm, "end": v(242.54, -35.98) * mm});
            skLineSegment(sketch, "E539", {"start": v(242.54, -35.98) * mm, "end": v(238.57, -35.98) * mm});
            skLineSegment(sketch, "E540", {"start": v(238.57, -35.98) * mm, "end": v(237.24, -35.98) * mm});
            skLineSegment(sketch, "E541", {"start": v(237.24, -35.98) * mm, "end": v(220.2, -35.98) * mm});
            skLineSegment(sketch, "E542", {"start": v(220.2, -35.98) * mm, "end": v(220, -35.03) * mm});
            skLineSegment(sketch, "E543", {"start": v(220, -35.03) * mm, "end": v(219.96, -34.89) * mm});
            skLineSegment(sketch, "E544", {"start": v(219.96, -34.89) * mm, "end": v(219.9, -34.4) * mm});
            skLineSegment(sketch, "E545", {"start": v(219.9, -34.4) * mm, "end": v(219.73, -33) * mm});
            skLineSegment(sketch, "E546", {"start": v(219.73, -33) * mm, "end": v(219.49, -30.9) * mm});
            skLineSegment(sketch, "E547", {"start": v(219.49, -30.9) * mm, "end": v(219.18, -28.2) * mm});
            skLineSegment(sketch, "E548", {"start": v(219.18, -28.2) * mm, "end": v(218.8, -25) * mm});
            skLineSegment(sketch, "E549", {"start": v(218.8, -25) * mm, "end": v(218.4, -21.38) * mm});
            skLineSegment(sketch, "E550", {"start": v(218.4, -21.38) * mm, "end": v(217.95, -17.42) * mm});
            skLineSegment(sketch, "E551", {"start": v(217.95, -17.42) * mm, "end": v(217.6, -14.28) * mm});
            skLineSegment(sketch, "E552", {"start": v(217.6, -14.28) * mm, "end": v(217.49, -13.23) * mm});
            skLineSegment(sketch, "E553", {"start": v(217.49, -13.23) * mm, "end": v(217.37, -12.18) * mm});
            skLineSegment(sketch, "E554", {"start": v(217.37, -12.18) * mm, "end": v(217, -9.03) * mm});
            skLineSegment(sketch, "E555", {"start": v(217, -9.03) * mm, "end": v(216.56, -5.1) * mm});
            skLineSegment(sketch, "E556", {"start": v(216.56, -5.1) * mm, "end": v(216.14, -1.51) * mm});
            skLineSegment(sketch, "E557", {"start": v(216.14, -1.51) * mm, "end": v(215.77, 1.64) * mm});
            skLineSegment(sketch, "E558", {"start": v(215.77, 1.64) * mm, "end": v(215.46, 4.26) * mm});
            skLineSegment(sketch, "E559", {"start": v(215.46, 4.26) * mm, "end": v(215.22, 6.27) * mm});
            skLineSegment(sketch, "E560", {"start": v(215.22, 6.27) * mm, "end": v(215.06, 7.59) * mm});
            skLineSegment(sketch, "E561", {"start": v(215.06, 7.59) * mm, "end": v(215, 8.04) * mm});
            skLineSegment(sketch, "E562", {"start": v(215, 8.04) * mm, "end": v(214.98, 8.11) * mm});
            skLineSegment(sketch, "E563", {"start": v(214.98, 8.11) * mm, "end": v(214.95, 8.2) * mm});
            skLineSegment(sketch, "E564", {"start": v(214.95, 8.2) * mm, "end": v(214.79, 8.44) * mm});
            skLineSegment(sketch, "E565", {"start": v(214.79, 8.44) * mm, "end": v(214.55, 8.23) * mm});
            skLineSegment(sketch, "E566", {"start": v(214.55, 8.23) * mm, "end": v(214.49, 8.15) * mm});
            skLineSegment(sketch, "E567", {"start": v(214.49, 8.15) * mm, "end": v(214.45, 8.08) * mm});
            skLineSegment(sketch, "E568", {"start": v(214.45, 8.08) * mm, "end": v(214.28, 7.6) * mm});
            skLineSegment(sketch, "E569", {"start": v(214.28, 7.6) * mm, "end": v(213.78, 6.23) * mm});
            skLineSegment(sketch, "E570", {"start": v(213.78, 6.23) * mm, "end": v(213.02, 4.13) * mm});
            skLineSegment(sketch, "E571", {"start": v(213.02, 4.13) * mm, "end": v(212.03, 1.4) * mm});
            skLineSegment(sketch, "E572", {"start": v(212.03, 1.4) * mm, "end": v(210.85, -1.9) * mm});
            skLineSegment(sketch, "E573", {"start": v(210.85, -1.9) * mm, "end": v(209.51, -5.64) * mm});
            skLineSegment(sketch, "E574", {"start": v(209.51, -5.64) * mm, "end": v(208.04, -9.76) * mm});
            skLineSegment(sketch, "E575", {"start": v(208.04, -9.76) * mm, "end": v(206.87, -13.05) * mm});
            skLineSegment(sketch, "E576", {"start": v(206.87, -13.05) * mm, "end": v(206.48, -14.15) * mm});
            skLineSegment(sketch, "E577", {"start": v(206.48, -14.15) * mm, "end": v(198.79, -35.98) * mm});
            skLineSegment(sketch, "E578", {"start": v(198.79, -35.98) * mm, "end": v(184.18, -35.98) * mm});
            skLineSegment(sketch, "E579", {"start": v(184.18, -35.98) * mm, "end": v(183.12, -35.98) * mm});
            skLineSegment(sketch, "E580", {"start": v(183.12, -35.98) * mm, "end": v(179.95, -35.98) * mm});
            skLineSegment(sketch, "E581", {"start": v(179.95, -35.98) * mm, "end": v(176.6, -35.97) * mm});
            skLineSegment(sketch, "E582", {"start": v(176.6, -35.97) * mm, "end": v(174.06, -35.94) * mm});
            skLineSegment(sketch, "E583", {"start": v(174.06, -35.94) * mm, "end": v(172.21, -35.9) * mm});
            skLineSegment(sketch, "E584", {"start": v(172.21, -35.9) * mm, "end": v(170.96, -35.83) * mm});
            skLineSegment(sketch, "E585", {"start": v(170.96, -35.83) * mm, "end": v(170.2, -35.74) * mm});
            skLineSegment(sketch, "E586", {"start": v(170.2, -35.74) * mm, "end": v(169.85, -35.63) * mm});
            skLineSegment(sketch, "E587", {"start": v(169.85, -35.63) * mm, "end": v(169.78, -35.52) * mm});
            skLineSegment(sketch, "E588", {"start": v(169.78, -35.52) * mm, "end": v(169.8, -35.49) * mm});
            skLineSegment(sketch, "E589", {"start": v(169.8, -35.49) * mm, "end": v(169.82, -35.42) * mm});
            skLineSegment(sketch, "E590", {"start": v(169.82, -35.42) * mm, "end": v(170.08, -34.67) * mm});
            skLineSegment(sketch, "E591", {"start": v(170.08, -34.67) * mm, "end": v(170.85, -32.53) * mm});
            skLineSegment(sketch, "E592", {"start": v(170.85, -32.53) * mm, "end": v(172.03, -29.2) * mm});
            skLineSegment(sketch, "E593", {"start": v(172.03, -29.2) * mm, "end": v(173.57, -24.85) * mm});
            skLineSegment(sketch, "E594", {"start": v(173.57, -24.85) * mm, "end": v(175.44, -19.6) * mm});
            skLineSegment(sketch, "E595", {"start": v(175.44, -19.6) * mm, "end": v(177.56, -13.62) * mm});
            skLineSegment(sketch, "E596", {"start": v(177.56, -13.62) * mm, "end": v(179.9, -7.03) * mm});
            skLineSegment(sketch, "E597", {"start": v(179.9, -7.03) * mm, "end": v(181.76, -1.76) * mm});
            skLineSegment(sketch, "E598", {"start": v(181.76, -1.76) * mm, "end": v(182.39, 0) * mm});
            skLineSegment(sketch, "E599", {"start": v(182.39, 0) * mm, "end": v(183, 1.76) * mm});
            skLineSegment(sketch, "E600", {"start": v(183, 1.76) * mm, "end": v(184.88, 7.03) * mm});
            skLineSegment(sketch, "E601", {"start": v(184.88, 7.03) * mm, "end": v(187.21, 13.62) * mm});
            skLineSegment(sketch, "E602", {"start": v(187.21, 13.62) * mm, "end": v(189.34, 19.6) * mm});
            skLineSegment(sketch, "E603", {"start": v(189.34, 19.6) * mm, "end": v(191.2, 24.85) * mm});
            skLineSegment(sketch, "E604", {"start": v(191.2, 24.85) * mm, "end": v(192.74, 29.2) * mm});
            skLineSegment(sketch, "E605", {"start": v(192.74, 29.2) * mm, "end": v(193.93, 32.53) * mm});
            skLineSegment(sketch, "E606", {"start": v(193.93, 32.53) * mm, "end": v(194.69, 34.67) * mm});
            skLineSegment(sketch, "E607", {"start": v(194.69, 34.67) * mm, "end": v(194.95, 35.42) * mm});
            skLineSegment(sketch, "E608", {"start": v(194.95, 35.42) * mm, "end": v(194.98, 35.5) * mm});
            skLineSegment(sketch, "E609", {"start": v(194.98, 35.5) * mm, "end": v(195, 35.54) * mm});
            skLineSegment(sketch, "E610", {"start": v(195, 35.54) * mm, "end": v(195.17, 35.63) * mm});
            skLineSegment(sketch, "E611", {"start": v(195.17, 35.63) * mm, "end": v(195.7, 35.75) * mm});
            skLineSegment(sketch, "E612", {"start": v(195.7, 35.75) * mm, "end": v(196.68, 35.83) * mm});
            skLineSegment(sketch, "E613", {"start": v(196.68, 35.83) * mm, "end": v(198.25, 35.9) * mm});
            skLineSegment(sketch, "E614", {"start": v(198.25, 35.9) * mm, "end": v(200.5, 35.94) * mm});
            skLineSegment(sketch, "E615", {"start": v(200.5, 35.94) * mm, "end": v(203.56, 35.97) * mm});
            skLineSegment(sketch, "E616", {"start": v(203.56, 35.97) * mm, "end": v(207.53, 35.98) * mm});
            skLineSegment(sketch, "E617", {"start": v(207.53, 35.98) * mm, "end": v(211.3, 35.98) * mm});
            skLineSegment(sketch, "E618", {"start": v(211.3, 35.98) * mm, "end": v(212.55, 35.98) * mm});
            skLineSegment(sketch, "E619", {"start": v(212.55, 35.98) * mm, "end": v(229.9, 35.98) * mm});
            skLineSegment(sketch, "E620", {"start": v(229.9, 35.98) * mm, "end": v(230.12, 34.5) * mm});
            skLineSegment(sketch, "E621", {"start": v(-132.57, 24.02) * mm, "end": v(-133.02, 23.87) * mm});
            skLineSegment(sketch, "E622", {"start": v(-133.02, 23.87) * mm, "end": v(-134.3, 23.27) * mm});
            skLineSegment(sketch, "E623", {"start": v(-134.3, 23.27) * mm, "end": v(-135.9, 22.2) * mm});
            skLineSegment(sketch, "E624", {"start": v(-135.9, 22.2) * mm, "end": v(-137.4, 20.75) * mm});
            skLineSegment(sketch, "E625", {"start": v(-137.4, 20.75) * mm, "end": v(-138.84, 18.88) * mm});
            skLineSegment(sketch, "E626", {"start": v(-138.84, 18.88) * mm, "end": v(-140.28, 16.5) * mm});
            skLineSegment(sketch, "E627", {"start": v(-140.28, 16.5) * mm, "end": v(-141.74, 13.58) * mm});
            skLineSegment(sketch, "E628", {"start": v(-141.74, 13.58) * mm, "end": v(-143.27, 10.04) * mm});
            skLineSegment(sketch, "E629", {"start": v(-143.27, 10.04) * mm, "end": v(-144.52, 6.88) * mm});
            skLineSegment(sketch, "E630", {"start": v(-144.52, 6.88) * mm, "end": v(-144.92, 5.82) * mm});
            skLineSegment(sketch, "E631", {"start": v(-144.92, 5.82) * mm, "end": v(-145.38, 4.61) * mm});
            skLineSegment(sketch, "E632", {"start": v(-145.38, 4.61) * mm, "end": v(-146.71, 0.98) * mm});
            skLineSegment(sketch, "E633", {"start": v(-146.71, 0.98) * mm, "end": v(-148.23, -3.3) * mm});
            skLineSegment(sketch, "E634", {"start": v(-148.23, -3.3) * mm, "end": v(-149.48, -7.03) * mm});
            skLineSegment(sketch, "E635", {"start": v(-149.48, -7.03) * mm, "end": v(-150.47, -10.26) * mm});
            skLineSegment(sketch, "E636", {"start": v(-150.47, -10.26) * mm, "end": v(-151.23, -13.05) * mm});
            skLineSegment(sketch, "E637", {"start": v(-151.23, -13.05) * mm, "end": v(-151.76, -15.41) * mm});
            skLineSegment(sketch, "E638", {"start": v(-151.76, -15.41) * mm, "end": v(-152.08, -17.4) * mm});
            skLineSegment(sketch, "E639", {"start": v(-152.08, -17.4) * mm, "end": v(-152.19, -18.64) * mm});
            skLineSegment(sketch, "E640", {"start": v(-152.19, -18.64) * mm, "end": v(-152.19, -19.05) * mm});
            skLineSegment(sketch, "E641", {"start": v(-152.19, -19.05) * mm, "end": v(-152.2, -19.74) * mm});
            skLineSegment(sketch, "E642", {"start": v(-152.2, -19.74) * mm, "end": v(-151.88, -21.82) * mm});
            skLineSegment(sketch, "E643", {"start": v(-151.88, -21.82) * mm, "end": v(-150.74, -23.6) * mm});
            skLineSegment(sketch, "E644", {"start": v(-150.74, -23.6) * mm, "end": v(-148.58, -24.54) * mm});
            skLineSegment(sketch, "E645", {"start": v(-148.58, -24.54) * mm, "end": v(-146.02, -24.83) * mm});
            skLineSegment(sketch, "E646", {"start": v(-146.02, -24.83) * mm, "end": v(-145.17, -24.83) * mm});
            skLineSegment(sketch, "E647", {"start": v(-145.17, -24.83) * mm, "end": v(-144.42, -24.83) * mm});
            skLineSegment(sketch, "E648", {"start": v(-144.42, -24.83) * mm, "end": v(-142.17, -24.68) * mm});
            skLineSegment(sketch, "E649", {"start": v(-142.17, -24.68) * mm, "end": v(-139.85, -24.12) * mm});
            skLineSegment(sketch, "E650", {"start": v(-139.85, -24.12) * mm, "end": v(-137.85, -23) * mm});
            skLineSegment(sketch, "E651", {"start": v(-137.85, -23) * mm, "end": v(-136.3, -21.68) * mm});
            skLineSegment(sketch, "E652", {"start": v(-136.3, -21.68) * mm, "end": v(-135.82, -21.2) * mm});
            skLineSegment(sketch, "E653", {"start": v(-135.82, -21.2) * mm, "end": v(-135.48, -20.86) * mm});
            skLineSegment(sketch, "E654", {"start": v(-135.48, -20.86) * mm, "end": v(-134.54, -19.75) * mm});
            skLineSegment(sketch, "E655", {"start": v(-134.54, -19.75) * mm, "end": v(-133.29, -17.97) * mm});
            skLineSegment(sketch, "E656", {"start": v(-133.29, -17.97) * mm, "end": v(-132.02, -15.78) * mm});
            skLineSegment(sketch, "E657", {"start": v(-132.02, -15.78) * mm, "end": v(-130.71, -13.08) * mm});
            skLineSegment(sketch, "E658", {"start": v(-130.71, -13.08) * mm, "end": v(-129.3, -9.8) * mm});
            skLineSegment(sketch, "E659", {"start": v(-129.3, -9.8) * mm, "end": v(-127.77, -5.84) * mm});
            skLineSegment(sketch, "E660", {"start": v(-127.77, -5.84) * mm, "end": v(-126.06, -1.1) * mm});
            skLineSegment(sketch, "E661", {"start": v(-126.06, -1.1) * mm, "end": v(-124.61, 3.08) * mm});
            skLineSegment(sketch, "E662", {"start": v(-124.61, 3.08) * mm, "end": v(-124.14, 4.48) * mm});
            skLineSegment(sketch, "E663", {"start": v(-124.14, 4.48) * mm, "end": v(-123.7, 5.78) * mm});
            skLineSegment(sketch, "E664", {"start": v(-123.7, 5.78) * mm, "end": v(-122.44, 9.7) * mm});
            skLineSegment(sketch, "E665", {"start": v(-122.44, 9.7) * mm, "end": v(-121.33, 13.57) * mm});
            skLineSegment(sketch, "E666", {"start": v(-121.33, 13.57) * mm, "end": v(-120.73, 16.5) * mm});
            skLineSegment(sketch, "E667", {"start": v(-120.73, 16.5) * mm, "end": v(-120.52, 18.28) * mm});
            skLineSegment(sketch, "E668", {"start": v(-120.52, 18.28) * mm, "end": v(-120.51, 18.87) * mm});
            skLineSegment(sketch, "E669", {"start": v(-120.51, 18.87) * mm, "end": v(-120.5, 19.36) * mm});
            skLineSegment(sketch, "E670", {"start": v(-120.5, 19.36) * mm, "end": v(-120.62, 20.8) * mm});
            skLineSegment(sketch, "E671", {"start": v(-120.62, 20.8) * mm, "end": v(-121.05, 22.2) * mm});
            skLineSegment(sketch, "E672", {"start": v(-121.05, 22.2) * mm, "end": v(-121.89, 23.23) * mm});
            skLineSegment(sketch, "E673", {"start": v(-121.89, 23.23) * mm, "end": v(-122.87, 23.86) * mm});
            skLineSegment(sketch, "E674", {"start": v(-122.87, 23.86) * mm, "end": v(-123.23, 24.02) * mm});
            skLineSegment(sketch, "E675", {"start": v(-123.23, 24.02) * mm, "end": v(-123.68, 24.22) * mm});
            skLineSegment(sketch, "E676", {"start": v(-123.68, 24.22) * mm, "end": v(-125.17, 24.52) * mm});
            skLineSegment(sketch, "E677", {"start": v(-125.17, 24.52) * mm, "end": v(-127.68, 24.69) * mm});
            skLineSegment(sketch, "E678", {"start": v(-127.68, 24.69) * mm, "end": v(-130.3, 24.52) * mm});
            skLineSegment(sketch, "E679", {"start": v(-130.3, 24.52) * mm, "end": v(-132.03, 24.21) * mm});
            skLineSegment(sketch, "E680", {"start": v(-132.03, 24.21) * mm, "end": v(-132.57, 24.02) * mm});
            skLineSegment(sketch, "E681", {"start": v(-41.45, 24.24) * mm, "end": v(-42, 24.05) * mm});
            skLineSegment(sketch, "E682", {"start": v(-42, 24.05) * mm, "end": v(-43.63, 23.33) * mm});
            skLineSegment(sketch, "E683", {"start": v(-43.63, 23.33) * mm, "end": v(-45.56, 22.05) * mm});
            skLineSegment(sketch, "E684", {"start": v(-45.56, 22.05) * mm, "end": v(-47.35, 20.24) * mm});
            skLineSegment(sketch, "E685", {"start": v(-47.35, 20.24) * mm, "end": v(-49.08, 17.72) * mm});
            skLineSegment(sketch, "E686", {"start": v(-49.08, 17.72) * mm, "end": v(-50.86, 14.35) * mm});
            skLineSegment(sketch, "E687", {"start": v(-50.86, 14.35) * mm, "end": v(-52.77, 9.97) * mm});
            skLineSegment(sketch, "E688", {"start": v(-52.77, 9.97) * mm, "end": v(-54.92, 4.42) * mm});
            skLineSegment(sketch, "E689", {"start": v(-54.92, 4.42) * mm, "end": v(-56.8, -0.74) * mm});
            skLineSegment(sketch, "E690", {"start": v(-56.8, -0.74) * mm, "end": v(-57.4, -2.47) * mm});
            skLineSegment(sketch, "E691", {"start": v(-57.4, -2.47) * mm, "end": v(-57.94, -4) * mm});
            skLineSegment(sketch, "E692", {"start": v(-57.94, -4) * mm, "end": v(-59.47, -8.66) * mm});
            skLineSegment(sketch, "E693", {"start": v(-59.47, -8.66) * mm, "end": v(-60.88, -13.64) * mm});
            skLineSegment(sketch, "E694", {"start": v(-60.88, -13.64) * mm, "end": v(-61.61, -17.54) * mm});
            skLineSegment(sketch, "E695", {"start": v(-61.61, -17.54) * mm, "end": v(-61.66, -20.47) * mm});
            skLineSegment(sketch, "E696", {"start": v(-61.66, -20.47) * mm, "end": v(-61, -22.55) * mm});
            skLineSegment(sketch, "E697", {"start": v(-61, -22.55) * mm, "end": v(-59.64, -23.89) * mm});
            skLineSegment(sketch, "E698", {"start": v(-59.64, -23.89) * mm, "end": v(-57.53, -24.6) * mm});
            skLineSegment(sketch, "E699", {"start": v(-57.53, -24.6) * mm, "end": v(-55.4, -24.8) * mm});
            skLineSegment(sketch, "E700", {"start": v(-55.4, -24.8) * mm, "end": v(-54.68, -24.8) * mm});
            skLineSegment(sketch, "E701", {"start": v(-54.68, -24.8) * mm, "end": v(-54.08, -24.8) * mm});
            skLineSegment(sketch, "E702", {"start": v(-54.08, -24.8) * mm, "end": v(-52.3, -24.7) * mm});
            skLineSegment(sketch, "E703", {"start": v(-52.3, -24.7) * mm, "end": v(-50.37, -24.38) * mm});
            skLineSegment(sketch, "E704", {"start": v(-50.37, -24.38) * mm, "end": v(-48.7, -23.77) * mm});
            skLineSegment(sketch, "E705", {"start": v(-48.7, -23.77) * mm, "end": v(-47.45, -23.09) * mm});
            skLineSegment(sketch, "E706", {"start": v(-47.45, -23.09) * mm, "end": v(-47.06, -22.82) * mm});
            skLineSegment(sketch, "E707", {"start": v(-47.06, -22.82) * mm, "end": v(-46.38, -22.37) * mm});
            skLineSegment(sketch, "E708", {"start": v(-46.38, -22.37) * mm, "end": v(-44.6, -20.59) * mm});
            skLineSegment(sketch, "E709", {"start": v(-44.6, -20.59) * mm, "end": v(-42.22, -17.08) * mm});
            skLineSegment(sketch, "E710", {"start": v(-42.22, -17.08) * mm, "end": v(-39.73, -11.98) * mm});
            skLineSegment(sketch, "E711", {"start": v(-39.73, -11.98) * mm, "end": v(-37.6, -6.71) * mm});
            skLineSegment(sketch, "E712", {"start": v(-37.6, -6.71) * mm, "end": v(-36.94, -4.94) * mm});
            skLineSegment(sketch, "E713", {"start": v(-36.94, -4.94) * mm, "end": v(-36.3, -3.19) * mm});
            skLineSegment(sketch, "E714", {"start": v(-36.3, -3.19) * mm, "end": v(-34.4, 2.08) * mm});
            skLineSegment(sketch, "E715", {"start": v(-34.4, 2.08) * mm, "end": v(-32.47, 7.9) * mm});
            skLineSegment(sketch, "E716", {"start": v(-32.47, 7.9) * mm, "end": v(-31.1, 12.62) * mm});
            skLineSegment(sketch, "E717", {"start": v(-31.1, 12.62) * mm, "end": v(-30.29, 16.36) * mm});
            skLineSegment(sketch, "E718", {"start": v(-30.29, 16.36) * mm, "end": v(-30, 19.25) * mm});
            skLineSegment(sketch, "E719", {"start": v(-30, 19.25) * mm, "end": v(-30.25, 21.39) * mm});
            skLineSegment(sketch, "E720", {"start": v(-30.25, 21.39) * mm, "end": v(-30.99, 22.9) * mm});
            skLineSegment(sketch, "E721", {"start": v(-30.99, 22.9) * mm, "end": v(-31.87, 23.7) * mm});
            skLineSegment(sketch, "E722", {"start": v(-31.87, 23.7) * mm, "end": v(-32.2, 23.88) * mm});
            skLineSegment(sketch, "E723", {"start": v(-32.2, 23.88) * mm, "end": v(-32.58, 24.08) * mm});
            skLineSegment(sketch, "E724", {"start": v(-32.58, 24.08) * mm, "end": v(-34, 24.36) * mm});
            skLineSegment(sketch, "E725", {"start": v(-34, 24.36) * mm, "end": v(-36.63, 24.59) * mm});
            skLineSegment(sketch, "E726", {"start": v(-36.63, 24.59) * mm, "end": v(-39.37, 24.56) * mm});
            skLineSegment(sketch, "E727", {"start": v(-39.37, 24.56) * mm, "end": v(-40.96, 24.4) * mm});
            skLineSegment(sketch, "E728", {"start": v(-40.96, 24.4) * mm, "end": v(-41.45, 24.24) * mm});
            skLineSegment(sketch, "E729", {"start": v(-235.1, 2.79) * mm, "end": v(-235.45, 1.77) * mm});
            skLineSegment(sketch, "E730", {"start": v(-235.45, 1.77) * mm, "end": v(-236.53, -1.26) * mm});
            skLineSegment(sketch, "E731", {"start": v(-236.53, -1.26) * mm, "end": v(-237.9, -5.15) * mm});
            skLineSegment(sketch, "E732", {"start": v(-237.9, -5.15) * mm, "end": v(-239.2, -8.78) * mm});
            skLineSegment(sketch, "E733", {"start": v(-239.2, -8.78) * mm, "end": v(-240.36, -12.07) * mm});
            skLineSegment(sketch, "E734", {"start": v(-240.36, -12.07) * mm, "end": v(-241.37, -14.91) * mm});
            skLineSegment(sketch, "E735", {"start": v(-241.37, -14.91) * mm, "end": v(-242.19, -17.22) * mm});
            skLineSegment(sketch, "E736", {"start": v(-242.19, -17.22) * mm, "end": v(-242.79, -18.9) * mm});
            skLineSegment(sketch, "E737", {"start": v(-242.79, -18.9) * mm, "end": v(-243.05, -19.62) * mm});
            skLineSegment(sketch, "E738", {"start": v(-243.05, -19.62) * mm, "end": v(-243.13, -19.86) * mm});
            skLineSegment(sketch, "E739", {"start": v(-243.13, -19.86) * mm, "end": v(-244.12, -22.65) * mm});
            skLineSegment(sketch, "E740", {"start": v(-244.12, -22.65) * mm, "end": v(-237.7, -22.5) * mm});
            skLineSegment(sketch, "E741", {"start": v(-237.7, -22.5) * mm, "end": v(-236.84, -22.49) * mm});
            skLineSegment(sketch, "E742", {"start": v(-236.84, -22.49) * mm, "end": v(-234.26, -22.4) * mm});
            skLineSegment(sketch, "E743", {"start": v(-234.26, -22.4) * mm, "end": v(-232.03, -22.25) * mm});
            skLineSegment(sketch, "E744", {"start": v(-232.03, -22.25) * mm, "end": v(-230.53, -22) * mm});
            skLineSegment(sketch, "E745", {"start": v(-230.53, -22) * mm, "end": v(-229.58, -21.7) * mm});
            skLineSegment(sketch, "E746", {"start": v(-229.58, -21.7) * mm, "end": v(-229.27, -21.59) * mm});
            skLineSegment(sketch, "E747", {"start": v(-229.27, -21.59) * mm, "end": v(-228.8, -21.4) * mm});
            skLineSegment(sketch, "E748", {"start": v(-228.8, -21.4) * mm, "end": v(-227.44, -20.69) * mm});
            skLineSegment(sketch, "E749", {"start": v(-227.44, -20.69) * mm, "end": v(-225.78, -19.46) * mm});
            skLineSegment(sketch, "E750", {"start": v(-225.78, -19.46) * mm, "end": v(-224.22, -17.78) * mm});
            skLineSegment(sketch, "E751", {"start": v(-224.22, -17.78) * mm, "end": v(-222.7, -15.57) * mm});
            skLineSegment(sketch, "E752", {"start": v(-222.7, -15.57) * mm, "end": v(-221.16, -12.72) * mm});
            skLineSegment(sketch, "E753", {"start": v(-221.16, -12.72) * mm, "end": v(-219.54, -9.13) * mm});
            skLineSegment(sketch, "E754", {"start": v(-219.54, -9.13) * mm, "end": v(-217.79, -4.69) * mm});
            skLineSegment(sketch, "E755", {"start": v(-217.79, -4.69) * mm, "end": v(-216.3, -0.65) * mm});
            skLineSegment(sketch, "E756", {"start": v(-216.3, -0.65) * mm, "end": v(-215.83, 0.7) * mm});
            skLineSegment(sketch, "E757", {"start": v(-215.83, 0.7) * mm, "end": v(-215.45, 1.77) * mm});
            skLineSegment(sketch, "E758", {"start": v(-215.45, 1.77) * mm, "end": v(-214.37, 4.98) * mm});
            skLineSegment(sketch, "E759", {"start": v(-214.37, 4.98) * mm, "end": v(-213.23, 8.63) * mm});
            skLineSegment(sketch, "E760", {"start": v(-213.23, 8.63) * mm, "end": v(-212.4, 11.73) * mm});
            skLineSegment(sketch, "E761", {"start": v(-212.4, 11.73) * mm, "end": v(-211.9, 14.3) * mm});
            skLineSegment(sketch, "E762", {"start": v(-211.9, 14.3) * mm, "end": v(-211.7, 16.41) * mm});
            skLineSegment(sketch, "E763", {"start": v(-211.7, 16.41) * mm, "end": v(-211.78, 18.1) * mm});
            skLineSegment(sketch, "E764", {"start": v(-211.78, 18.1) * mm, "end": v(-212.16, 19.4) * mm});
            skLineSegment(sketch, "E765", {"start": v(-212.16, 19.4) * mm, "end": v(-212.63, 20.18) * mm});
            skLineSegment(sketch, "E766", {"start": v(-212.63, 20.18) * mm, "end": v(-212.83, 20.4) * mm});
            skLineSegment(sketch, "E767", {"start": v(-212.83, 20.4) * mm, "end": v(-213.1, 20.67) * mm});
            skLineSegment(sketch, "E768", {"start": v(-213.1, 20.67) * mm, "end": v(-214.04, 21.35) * mm});
            skLineSegment(sketch, "E769", {"start": v(-214.04, 21.35) * mm, "end": v(-215.72, 21.95) * mm});
            skLineSegment(sketch, "E770", {"start": v(-215.72, 21.95) * mm, "end": v(-218.3, 22.3) * mm});
            skLineSegment(sketch, "E771", {"start": v(-218.3, 22.3) * mm, "end": v(-221.26, 22.45) * mm});
            skLineSegment(sketch, "E772", {"start": v(-221.26, 22.45) * mm, "end": v(-222.25, 22.47) * mm});
            skLineSegment(sketch, "E773", {"start": v(-222.25, 22.47) * mm, "end": v(-228.07, 22.65) * mm});
            skLineSegment(sketch, "E774", {"start": v(-228.07, 22.65) * mm, "end": v(-235.1, 2.79) * mm});
            skLineSegment(sketch, "E775", {"start": v(127.21, 6.28) * mm, "end": v(126.73, 5.53) * mm});
            skLineSegment(sketch, "E776", {"start": v(126.73, 5.53) * mm, "end": v(125.3, 3.28) * mm});
            skLineSegment(sketch, "E777", {"start": v(125.3, 3.28) * mm, "end": v(123.52, 0.46) * mm});
            skLineSegment(sketch, "E778", {"start": v(123.52, 0.46) * mm, "end": v(121.9, -2.1) * mm});
            skLineSegment(sketch, "E779", {"start": v(121.9, -2.1) * mm, "end": v(120.48, -4.37) * mm});
            skLineSegment(sketch, "E780", {"start": v(120.48, -4.37) * mm, "end": v(119.3, -6.26) * mm});
            skLineSegment(sketch, "E781", {"start": v(119.3, -6.26) * mm, "end": v(118.4, -7.71) * mm});
            skLineSegment(sketch, "E782", {"start": v(118.4, -7.71) * mm, "end": v(117.8, -8.67) * mm});
            skLineSegment(sketch, "E783", {"start": v(117.8, -8.67) * mm, "end": v(117.6, -9) * mm});
            skLineSegment(sketch, "E784", {"start": v(117.6, -9) * mm, "end": v(117.58, -9.07) * mm});
            skLineSegment(sketch, "E785", {"start": v(117.58, -9.07) * mm, "end": v(117.57, -9.09) * mm});
            skLineSegment(sketch, "E786", {"start": v(117.57, -9.09) * mm, "end": v(117.86, -9.29) * mm});
            skLineSegment(sketch, "E787", {"start": v(117.86, -9.29) * mm, "end": v(119.17, -9.43) * mm});
            skLineSegment(sketch, "E788", {"start": v(119.17, -9.43) * mm, "end": v(121.83, -9.5) * mm});
            skLineSegment(sketch, "E789", {"start": v(121.83, -9.5) * mm, "end": v(125.1, -9.53) * mm});
            skLineSegment(sketch, "E790", {"start": v(125.1, -9.53) * mm, "end": v(126.19, -9.53) * mm});
            skLineSegment(sketch, "E791", {"start": v(126.19, -9.53) * mm, "end": v(134.97, -9.53) * mm});
            skLineSegment(sketch, "E792", {"start": v(134.97, -9.53) * mm, "end": v(135.92, 4.16) * mm});
            skLineSegment(sketch, "E793", {"start": v(135.92, 4.16) * mm, "end": v(136.03, 5.52) * mm});
            skLineSegment(sketch, "E794", {"start": v(136.03, 5.52) * mm, "end": v(136.33, 9.6) * mm});
            skLineSegment(sketch, "E795", {"start": v(136.33, 9.6) * mm, "end": v(136.7, 14.3) * mm});
            skLineSegment(sketch, "E796", {"start": v(136.7, 14.3) * mm, "end": v(136.97, 17.77) * mm});
            skLineSegment(sketch, "E797", {"start": v(136.97, 17.77) * mm, "end": v(137.1, 19.27) * mm});
            skLineSegment(sketch, "E798", {"start": v(137.1, 19.27) * mm, "end": v(137.12, 19.5) * mm});
            skLineSegment(sketch, "E799", {"start": v(137.12, 19.5) * mm, "end": v(137.15, 19.75) * mm});
            skLineSegment(sketch, "E800", {"start": v(137.15, 19.75) * mm, "end": v(137.17, 20.7) * mm});
            skLineSegment(sketch, "E801", {"start": v(137.17, 20.7) * mm, "end": v(137.03, 21.17) * mm});
            skLineSegment(sketch, "E802", {"start": v(137.03, 21.17) * mm, "end": v(136.98, 21.17) * mm});
            skLineSegment(sketch, "E803", {"start": v(136.98, 21.17) * mm, "end": v(136.92, 21.17) * mm});
            skLineSegment(sketch, "E804", {"start": v(136.92, 21.17) * mm, "end": v(136.72, 20.86) * mm});
            skLineSegment(sketch, "E805", {"start": v(136.72, 20.86) * mm, "end": v(136.11, 20) * mm});
            skLineSegment(sketch, "E806", {"start": v(136.11, 20) * mm, "end": v(135.18, 18.61) * mm});
            skLineSegment(sketch, "E807", {"start": v(135.18, 18.61) * mm, "end": v(133.97, 16.8) * mm});
            skLineSegment(sketch, "E808", {"start": v(133.97, 16.8) * mm, "end": v(132.53, 14.59) * mm});
            skLineSegment(sketch, "E809", {"start": v(132.53, 14.59) * mm, "end": v(130.9, 12.06) * mm});
            skLineSegment(sketch, "E810", {"start": v(130.9, 12.06) * mm, "end": v(129.11, 9.27) * mm});
            skLineSegment(sketch, "E811", {"start": v(129.11, 9.27) * mm, "end": v(127.69, 7.03) * mm});
            skLineSegment(sketch, "E812", {"start": v(127.69, 7.03) * mm, "end": v(127.21, 6.28) * mm});
            skLineSegment(sketch, "E813", {"start": v(-110.95, 36.65) * mm, "end": v(-105.6, 35.72) * mm});
            skSolve(sketch);
        }
        {
            var Q0;
            Q0 = qSketchRegion(id + "F0", true);
            extrude(context, id + "F1", {"entities" : qUnion([Q0]), "depth" : 6.35 * mm});
        }
    });
